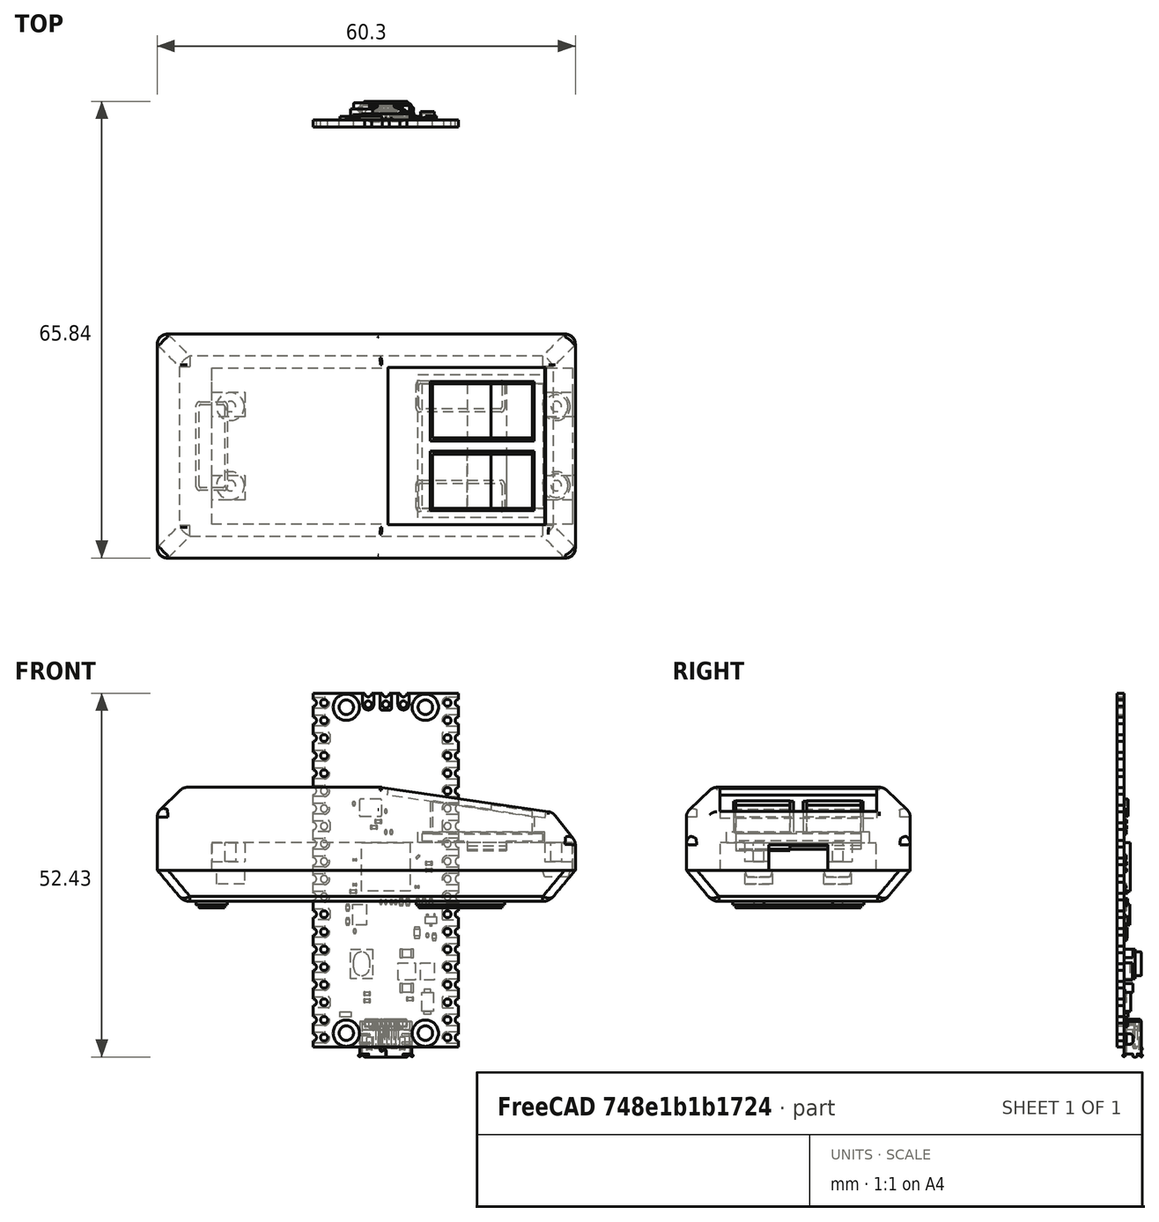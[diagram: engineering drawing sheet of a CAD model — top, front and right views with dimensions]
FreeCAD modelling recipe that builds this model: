
FCSTD DOCUMENT  (FreeCAD 0.22R36731 (Git))
Label: mouse
License: All rights reserved
LicenseURL: http://en.wikipedia.org/wiki/All_rights_reserved
objects: Part::Feature×116, App::Part×35, Sketcher::SketchObject×19, PartDesign::Pocket×11, PartDesign::Pad×8, PartDesign::Body×4, PartDesign::Fillet×2, Mesh::Feature×1, PartDesign::Plane×1
note: 182 computed .brp shape members not serialized (recipe doc carries the construction recipe); baked Part::Feature solids carry a one-line shape summary decoded from their .brp

FEATURE [Sketcher::SketchObject] Sketch
  AttachmentSupport = -> [XZ_Plane]
  FullyConstrained = true
  MapMode = 5
  Placement = pos=(0,0,0) rot=(1,0,0;1.5708rad)
  sketch-geometry (14):
    g0: LineSegment StartX=21.1514 StartY=8.48067 StartZ=0 EndX=15.1514 EndY=9.36067 EndZ=0
    g1: LineSegment StartX=15.1514 StartY=9.36067 StartZ=0 EndX=15.1514 EndY=8.76067 EndZ=0
    g2: LineSegment StartX=15.1514 StartY=8.76067 StartZ=0 EndX=6.70138 EndY=10 EndZ=0
    g3: LineSegment StartX=6.70138 StartY=10 StartZ=0 EndX=6.70138 EndY=5.25 EndZ=0
    g4: LineSegment StartX=6.70138 StartY=5.25 StartZ=0 EndX=5.20138 EndY=5.25 EndZ=0
    g5: LineSegment StartX=5.20138 StartY=5.25 StartZ=0 EndX=5.20138 EndY=4.25 EndZ=0
    g6: LineSegment StartX=5.20138 StartY=4.25 StartZ=0 EndX=11.74 EndY=4.25 EndZ=0
    g7: LineSegment StartX=11.74 StartY=4.25 StartZ=0 EndX=11.74 EndY=3 EndZ=0
    g8: LineSegment StartX=11.74 StartY=3 StartZ=0 EndX=17.37 EndY=3 EndZ=0
    g9: LineSegment StartX=17.37 StartY=3 StartZ=0 EndX=17.37 EndY=4.25 EndZ=0
    g10: LineSegment StartX=17.37 StartY=4.25 StartZ=0 EndX=22.6514 EndY=4.25 EndZ=0
    g11: LineSegment StartX=22.6514 StartY=4.25 StartZ=0 EndX=22.6514 EndY=5.25 EndZ=0
    g12: LineSegment StartX=22.6514 StartY=5.25 StartZ=0 EndX=21.1514 EndY=5.25 EndZ=0
    g13: LineSegment StartX=21.1514 StartY=5.25 StartZ=0 EndX=21.1514 EndY=8.48067 EndZ=0
  constraints (42):
    c: Coincident(g0,g1)
    c: Vertical(g1)
    c: Coincident(g1,g2)
    c: Coincident(g2,g3)
    c: Vertical(g3)
    c: Coincident(g3,g4)
    c: Coincident(g4,g5)
    c: Vertical(g5)
    c: Coincident(g5,g6)
    c: Horizontal(g6)
    c: Coincident(g6,g7)
    c: Coincident(g7,g8)
    c: Horizontal(g8)
    c: Coincident(g8,g9)
    c: Coincident(g9,g10)
    c: Coincident(g10,g11)
    c: Vertical(g11)
    c: Coincident(g11,g12)
    c: Coincident(g12,g13)
    c: Coincident(g13,g0)
    c: Vertical(g13)
    c: Parallel(g0,g2)
    c: DistanceX(g0) = 21.1514
    c: DistanceX(g0,g0) = 6
    c: DistanceX(g2,g2) = 8.45
    c: DistanceY(g0,g0) = 0.88
    c: DistanceY(g1,g1) = 0.6
    c: Vertical(g9)
    c: Vertical(g7)
    c: Horizontal(g10)
    c: Equal(g7,g9)
    c: DistanceX(g7) = 11.74
    c: DistanceX(g8,g8) = 5.63
    c: DistanceX(g4,g3) = 1.5
    c: DistanceY(g7) = 3
    c: Horizontal(g12)
    c: DistanceX(g12,g12) = 1.5
    c: Horizontal(g4)
    c: PointOnObject(g3,g12)
    c: DistanceY(g5,g5) = 1
    c: DistanceY(g7,g7) = 1.25
    c: DistanceY(g3,g3) = 4.75
FEATURE [PartDesign::Pad] Pad
  Direction = (0,-1,2e-16)
  Length = 18
  Length2 = 10
  Placement = pos=(0,0,0) rot=(1,0,0;1.5708rad)
  Profile = -> Sketch
  ReferenceAxis = -> Sketch [N_Axis]
  Refine = true
  Suppressed = false
  Type = 0
FEATURE [Mesh::Feature] mouse_bottom
FEATURE [Part::Feature] Part__Feature  label="PCB, Raspberry Pi Pico-R3"
  shape: bbox 21 x 1 x 51 mm, 416 faces (baked)
FEATURE [Part::Feature] Part__Feature001  label="MicroUSB Port, Raspberry Pi Pico-R3"
  Placement = pos=(0,0.5,-24.35) rot=(0,1,0;3.14159rad)
  shape: bbox 7.999 x 2.949 x 5.461 mm, 809 faces (baked)
FEATURE [Part::Feature] Part__Feature002  label="MicroUSB Port, Raspberry Pi Pico-R004"
  Placement = pos=(0,0.5,-24.35) rot=(0,1,0;3.14159rad)
  shape: bbox 6.982 x 2.155 x 3.937 mm, 206 faces (baked)
FEATURE [Part::Feature] Part__Feature003  label="MicroUSB Port, Raspberry Pi Pico-R005"
  Placement = pos=(0,0.5,-24.35) rot=(0,1,0;3.14159rad)
  shape: bbox 0.37 x 1.716 x 4 mm, 43 faces (baked)
FEATURE [Part::Feature] Part__Feature004  label="MicroUSB Port, Raspberry Pi Pico-R006"
  Placement = pos=(0,0.5,-24.35) rot=(0,1,0;3.14159rad)
  shape: bbox 0.37 x 1.716 x 4 mm, 43 faces (baked)
FEATURE [Part::Feature] Part__Feature005  label="MicroUSB Port, Raspberry Pi Pico-R007"
  Placement = pos=(0,0.5,-24.35) rot=(0,1,0;3.14159rad)
  shape: bbox 0.37 x 1.716 x 4 mm, 43 faces (baked)
FEATURE [Part::Feature] Part__Feature006  label="MicroUSB Port, Raspberry Pi Pico-R008"
  Placement = pos=(0,0.5,-24.35) rot=(0,1,0;3.14159rad)
  shape: bbox 0.37 x 1.716 x 4 mm, 43 faces (baked)
FEATURE [Part::Feature] Part__Feature007  label="MicroUSB Port, Raspberry Pi Pico-R009"
  Placement = pos=(0,0.5,-24.35) rot=(0,1,0;3.14159rad)
  shape: bbox 0.37 x 1.716 x 4 mm, 43 faces (baked)
FEATURE [App::Part] MicroUSB_Port__Raspberry_Pi_Pico_R3  label="MicroUSB Port, Raspberry Pi Pico-R010"
  Group = -> [Part__Feature001,Part__Feature002,Part__Feature003,Part__Feature004,Part__Feature005,Part__Feature006,Part__Feature007]
  Origin = -> Origin001
FEATURE [Part::Feature] Part__Feature008  label="RP2040 Microcontroller, Raspberry Pi Pico-R3"
  Placement = pos=(0,0.5,0.5) rot=(0,0,1;0rad)
  shape: bbox 7 x 0.9 x 7 mm, 6 faces (baked)
FEATURE [Part::Feature] Part__Feature009  label="SW1, Tact Switch, Raspberry Pi Pico-R3"
  Placement = pos=(-3.5,0.5,-13.5) rot=(0,0,1;0rad)
  shape: bbox 3.2 x 2.5 x 4.25 mm, 17 faces (baked)
FEATURE [Part::Feature] Part__Feature010  label="D1, Diode, Schottky, Raspberry Pi Pico-R3"
  Placement = pos=(6,0.5,-19) rot=(0,0,1;0rad)
  shape: bbox 1.65 x 0.95 x 3.6 mm, 14 faces (baked)
FEATURE [Part::Feature] Part__Feature011  label="D2, QSME-C194, LED, Raspberry Pi Pico-R3"
  Placement = pos=(-5.8,0.5,-20.8) rot=(0,0,1;0rad)
  shape: bbox 1.6 x 0.55 x 0.8 mm, 6 faces (baked)
FEATURE [Part::Feature] Part__Feature012  label="L1, Inductor, Raspberry Pi Pico-R3"
  Placement = pos=(6,0.5,-14.6) rot=(0,0,1;0rad)
  shape: bbox 2 x 1.2 x 2.5 mm, 6 faces (baked)
FEATURE [Part::Feature] Part__Feature013  label="U2, RT6150B-33GQW, Buck Boost Converter, Raspberry Pi Pico-R3"
  Placement = pos=(3,0.5,-14.6) rot=(0,0,1;0rad)
  shape: bbox 2.5 x 0.8 x 2.5 mm, 6 faces (baked)
FEATURE [Part::Feature] Part__Feature014  label="U3, W25Q16JVUXIQ, Serial NOR Flash 16 Mbit, Raspberry Pi Pico-R3"
  Placement = pos=(-3.8,0.5,-6.4) rot=(0,0,1;0rad)
  shape: bbox 2 x 0.8 x 3 mm, 6 faces (baked)
FEATURE [Part::Feature] Part__Feature015  label="Q1, MOSFET, DMG1012T, Raspberry Pi Pico-R3"
  Placement = pos=(6.5,0.5,-7.2) rot=(0,0,1;0rad)
  shape: bbox 1.6 x 0.6 x 1.8 mm, 18 faces (baked)
FEATURE [Part::Feature] Part__Feature016  label="X1, X12M000000S096, 12 Mhz Crystal Resonator, Raspberry Pi Pico-R3"
  Placement = pos=(-2.2,0.5,9) rot=(0,0,1;0rad)
  shape: bbox 3.2 x 0.6 x 2.5 mm, 18 faces (baked)
FEATURE [Part::Feature] Part__Feature017  label="SMD Resistor, Configurable, Raspberry Pi Pico-R3_R1"
  Placement = pos=(6.2,0.5,1) rot=(0,1,0;1.5708rad)
  shape: bbox 0.6 x 0.35 x 0.5 mm, 6 faces (baked)
FEATURE [Part::Feature] Part__Feature018  label="SMD Resistor, Configurable, Raspberry Pi Pico-R3_R002"
  Placement = pos=(6.2,0.5,1) rot=(0,1,0;1.5708rad)
  shape: bbox 0.2 x 0.35 x 0.5 mm, 6 faces (baked)
FEATURE [Part::Feature] Part__Feature019  label="SMD Resistor, Configurable, Raspberry Pi Pico-R3_R003"
  Placement = pos=(6.2,0.5,1) rot=(0,1,0;1.5708rad)
  shape: bbox 0.2 x 0.35 x 0.5 mm, 6 faces (baked)
FEATURE [App::Part] SMD_Resistor__Configurable__Raspberry_Pi_Pico_R3_R1  label="SMD Resistor, Configurable, Raspberry Pi Pico-R3_R004"
  Group = -> [Part__Feature017,Part__Feature018,Part__Feature019]
  Origin = -> Origin002
FEATURE [Part::Feature] Part__Feature020  label="SMD Resistor, Configurable, Raspberry Pi Pico-R3_R2"
  Placement = pos=(3.5,0.5,-18.6) rot=(0,1,0;1.5708rad)
  shape: bbox 0.6 x 0.35 x 0.5 mm, 6 faces (baked)
FEATURE [Part::Feature] Part__Feature021  label="SMD Resistor, Configurable, Raspberry Pi Pico-R3_R005"
  Placement = pos=(3.5,0.5,-18.6) rot=(0,1,0;1.5708rad)
  shape: bbox 0.2 x 0.35 x 0.5 mm, 6 faces (baked)
FEATURE [Part::Feature] Part__Feature022  label="SMD Resistor, Configurable, Raspberry Pi Pico-R3_R006"
  Placement = pos=(3.5,0.5,-18.6) rot=(0,1,0;1.5708rad)
  shape: bbox 0.2 x 0.35 x 0.5 mm, 6 faces (baked)
FEATURE [App::Part] SMD_Resistor__Configurable__Raspberry_Pi_Pico_R3_R2  label="SMD Resistor, Configurable, Raspberry Pi Pico-R3_R007"
  Group = -> [Part__Feature020,Part__Feature021,Part__Feature022]
  Origin = -> Origin003
FEATURE [Part::Feature] Part__Feature023  label="SMD Resistor, Configurable, Raspberry Pi Pico-R3_R3"
  Placement = pos=(-2.7,0.5,-17.8) rot=(0,1,0;1.5708rad)
  shape: bbox 0.6 x 0.35 x 0.5 mm, 6 faces (baked)
FEATURE [Part::Feature] Part__Feature024  label="SMD Resistor, Configurable, Raspberry Pi Pico-R3_R008"
  Placement = pos=(-2.7,0.5,-17.8) rot=(0,1,0;1.5708rad)
  shape: bbox 0.2 x 0.35 x 0.5 mm, 6 faces (baked)
FEATURE [Part::Feature] Part__Feature025  label="SMD Resistor, Configurable, Raspberry Pi Pico-R3_R009"
  Placement = pos=(-2.7,0.5,-17.8) rot=(0,1,0;1.5708rad)
  shape: bbox 0.2 x 0.35 x 0.5 mm, 6 faces (baked)
FEATURE [App::Part] SMD_Resistor__Configurable__Raspberry_Pi_Pico_R3_R3  label="SMD Resistor, Configurable, Raspberry Pi Pico-R3_R010"
  Group = -> [Part__Feature023,Part__Feature024,Part__Feature025]
  Origin = -> Origin004
FEATURE [Part::Feature] Part__Feature026  label="SMD Resistor, Configurable, Raspberry Pi Pico-R3_R4"
  Placement = pos=(-5.5,0.5,-5.4) rot=(0,1,0;3.14159rad)
  shape: bbox 0.5 x 0.35 x 0.6 mm, 6 faces (baked)
FEATURE [Part::Feature] Part__Feature027  label="SMD Resistor, Configurable, Raspberry Pi Pico-R3_R011"
  Placement = pos=(-5.5,0.5,-5.4) rot=(0,1,0;3.14159rad)
  shape: bbox 0.5 x 0.35 x 0.2 mm, 6 faces (baked)
FEATURE [Part::Feature] Part__Feature028  label="SMD Resistor, Configurable, Raspberry Pi Pico-R3_R012"
  Placement = pos=(-5.5,0.5,-5.4) rot=(0,1,0;3.14159rad)
  shape: bbox 0.5 x 0.35 x 0.2 mm, 6 faces (baked)
FEATURE [App::Part] SMD_Resistor__Configurable__Raspberry_Pi_Pico_R3_R4  label="SMD Resistor, Configurable, Raspberry Pi Pico-R3_R013"
  Group = -> [Part__Feature026,Part__Feature027,Part__Feature028]
  Origin = -> Origin005
FEATURE [Part::Feature] Part__Feature029  label="SMD Resistor, Configurable, Raspberry Pi Pico-R3_R5"
  Placement = pos=(7,0.5,-9.6) rot=(0,1,0;3.14159rad)
  shape: bbox 0.5 x 0.35 x 0.6 mm, 6 faces (baked)
FEATURE [Part::Feature] Part__Feature030  label="SMD Resistor, Configurable, Raspberry Pi Pico-R3_R014"
  Placement = pos=(7,0.5,-9.6) rot=(0,1,0;3.14159rad)
  shape: bbox 0.5 x 0.35 x 0.2 mm, 6 faces (baked)
FEATURE [Part::Feature] Part__Feature031  label="SMD Resistor, Configurable, Raspberry Pi Pico-R3_R015"
  Placement = pos=(7,0.5,-9.6) rot=(0,1,0;3.14159rad)
  shape: bbox 0.5 x 0.35 x 0.2 mm, 6 faces (baked)
FEATURE [App::Part] SMD_Resistor__Configurable__Raspberry_Pi_Pico_R3_R5  label="SMD Resistor, Configurable, Raspberry Pi Pico-R3_R016"
  Group = -> [Part__Feature029,Part__Feature030,Part__Feature031]
  Origin = -> Origin006
FEATURE [Part::Feature] Part__Feature032  label="SMD Resistor, Configurable, Raspberry Pi Pico-R3_R6"
  Placement = pos=(6.5,0.5,-4.6) rot=(0,1,0;3.14159rad)
  shape: bbox 0.5 x 0.35 x 0.6 mm, 6 faces (baked)
FEATURE [Part::Feature] Part__Feature033  label="SMD Resistor, Configurable, Raspberry Pi Pico-R3_R017"
  Placement = pos=(6.5,0.5,-4.6) rot=(0,1,0;3.14159rad)
  shape: bbox 0.5 x 0.35 x 0.2 mm, 6 faces (baked)
FEATURE [Part::Feature] Part__Feature034  label="SMD Resistor, Configurable, Raspberry Pi Pico-R3_R018"
  Placement = pos=(6.5,0.5,-4.6) rot=(0,1,0;3.14159rad)
  shape: bbox 0.5 x 0.35 x 0.2 mm, 6 faces (baked)
FEATURE [App::Part] SMD_Resistor__Configurable__Raspberry_Pi_Pico_R3_R6  label="SMD Resistor, Configurable, Raspberry Pi Pico-R3_R019"
  Group = -> [Part__Feature032,Part__Feature033,Part__Feature034]
  Origin = -> Origin007
FEATURE [Part::Feature] Part__Feature035  label="SMD Resistor, Configurable, Raspberry Pi Pico-R3_R7"
  Placement = pos=(4.5,0.5,-9) rot=(0,1,0;3.14159rad)
  shape: bbox 0.8 x 0.45 x 1 mm, 6 faces (baked)
FEATURE [Part::Feature] Part__Feature036  label="SMD Resistor, Configurable, Raspberry Pi Pico-R3_R020"
  Placement = pos=(4.5,0.5,-9) rot=(0,1,0;3.14159rad)
  shape: bbox 0.8 x 0.45 x 0.3 mm, 6 faces (baked)
FEATURE [Part::Feature] Part__Feature037  label="SMD Resistor, Configurable, Raspberry Pi Pico-R3_R021"
  Placement = pos=(4.5,0.5,-9) rot=(0,1,0;3.14159rad)
  shape: bbox 0.8 x 0.45 x 0.3 mm, 6 faces (baked)
FEATURE [App::Part] SMD_Resistor__Configurable__Raspberry_Pi_Pico_R3_R7  label="SMD Resistor, Configurable, Raspberry Pi Pico-R3_R022"
  Group = -> [Part__Feature035,Part__Feature036,Part__Feature037]
  Origin = -> Origin008
FEATURE [Part::Feature] Part__Feature038  label="SMD Resistor, Configurable, Raspberry Pi Pico-R3_R8"
  Placement = pos=(-2.7,0.5,-18.8) rot=(0,1,0;1.5708rad)
  shape: bbox 0.6 x 0.35 x 0.5 mm, 6 faces (baked)
FEATURE [Part::Feature] Part__Feature039  label="SMD Resistor, Configurable, Raspberry Pi Pico-R3_R023"
  Placement = pos=(-2.7,0.5,-18.8) rot=(0,1,0;1.5708rad)
  shape: bbox 0.2 x 0.35 x 0.5 mm, 6 faces (baked)
FEATURE [Part::Feature] Part__Feature040  label="SMD Resistor, Configurable, Raspberry Pi Pico-R3_R024"
  Placement = pos=(-2.7,0.5,-18.8) rot=(0,1,0;1.5708rad)
  shape: bbox 0.2 x 0.35 x 0.5 mm, 6 faces (baked)
FEATURE [App::Part] SMD_Resistor__Configurable__Raspberry_Pi_Pico_R3_R8  label="SMD Resistor, Configurable, Raspberry Pi Pico-R3_R025"
  Group = -> [Part__Feature038,Part__Feature039,Part__Feature040]
  Origin = -> Origin009
FEATURE [Part::Feature] Part__Feature041  label="SMD Resistor, Configurable, Raspberry Pi Pico-R3_R9"
  Placement = pos=(5.5,0.5,-4.6) rot=(0,1,0;3.14159rad)
  shape: bbox 0.5 x 0.35 x 0.6 mm, 6 faces (baked)
FEATURE [Part::Feature] Part__Feature042  label="SMD Resistor, Configurable, Raspberry Pi Pico-R3_R026"
  Placement = pos=(5.5,0.5,-4.6) rot=(0,1,0;3.14159rad)
  shape: bbox 0.5 x 0.35 x 0.2 mm, 6 faces (baked)
FEATURE [Part::Feature] Part__Feature043  label="SMD Resistor, Configurable, Raspberry Pi Pico-R3_R027"
  Placement = pos=(5.5,0.5,-4.6) rot=(0,1,0;3.14159rad)
  shape: bbox 0.5 x 0.35 x 0.2 mm, 6 faces (baked)
FEATURE [App::Part] SMD_Resistor__Configurable__Raspberry_Pi_Pico_R3_R9  label="SMD Resistor, Configurable, Raspberry Pi Pico-R3_R028"
  Group = -> [Part__Feature041,Part__Feature042,Part__Feature043]
  Origin = -> Origin010
FEATURE [Part::Feature] Part__Feature044  label="SMD Resistor, Configurable, Raspberry Pi Pico-R3_R10"
  Placement = pos=(6.2,0.5,-1e-16) rot=(0,1,0;1.5708rad)
  shape: bbox 0.6 x 0.35 x 0.5 mm, 6 faces (baked)
FEATURE [Part::Feature] Part__Feature045  label="SMD Resistor, Configurable, Raspberry Pi Pico-R3_R029"
  Placement = pos=(6.2,0.5,-1e-16) rot=(0,1,0;1.5708rad)
  shape: bbox 0.2 x 0.35 x 0.5 mm, 6 faces (baked)
FEATURE [Part::Feature] Part__Feature046  label="SMD Resistor, Configurable, Raspberry Pi Pico-R3_R030"
  Placement = pos=(6.2,0.5,-1e-16) rot=(0,1,0;1.5708rad)
  shape: bbox 0.2 x 0.35 x 0.5 mm, 6 faces (baked)
FEATURE [App::Part] SMD_Resistor__Configurable__Raspberry_Pi_Pico_R3_R10  label="SMD Resistor, Configurable, Raspberry Pi Pico-R3_R031"
  Group = -> [Part__Feature044,Part__Feature045,Part__Feature046]
  Origin = -> Origin011
FEATURE [Part::Feature] Part__Feature047  label="SMD Resistor, Configurable, Raspberry Pi Pico-R3_R11"
  Placement = pos=(-5.5,0.5,-7.4) rot=(0,0,1;0rad)
  shape: bbox 0.5 x 0.35 x 0.6 mm, 6 faces (baked)
FEATURE [Part::Feature] Part__Feature048  label="SMD Resistor, Configurable, Raspberry Pi Pico-R3_R032"
  Placement = pos=(-5.5,0.5,-7.4) rot=(0,0,1;0rad)
  shape: bbox 0.5 x 0.35 x 0.2 mm, 6 faces (baked)
FEATURE [Part::Feature] Part__Feature049  label="SMD Resistor, Configurable, Raspberry Pi Pico-R3_R033"
  Placement = pos=(-5.5,0.5,-7.4) rot=(0,0,1;0rad)
  shape: bbox 0.5 x 0.35 x 0.2 mm, 6 faces (baked)
FEATURE [App::Part] SMD_Resistor__Configurable__Raspberry_Pi_Pico_R3_R11  label="SMD Resistor, Configurable, Raspberry Pi Pico-R3_R034"
  Group = -> [Part__Feature047,Part__Feature048,Part__Feature049]
  Origin = -> Origin012
FEATURE [Part::Feature] Part__Feature050  label="SMD Resistor, Configurable, Raspberry Pi Pico-R3_R12"
  Placement = pos=(0.8,0.5,-4.6) rot=(0,1,0;3.14159rad)
  shape: bbox 0.3 x 0.23 x 0.4 mm, 6 faces (baked)
FEATURE [Part::Feature] Part__Feature051  label="SMD Resistor, Configurable, Raspberry Pi Pico-R3_R035"
  Placement = pos=(0.8,0.5,-4.6) rot=(0,1,0;3.14159rad)
  shape: bbox 0.3 x 0.23 x 0.1 mm, 6 faces (baked)
FEATURE [Part::Feature] Part__Feature052  label="SMD Resistor, Configurable, Raspberry Pi Pico-R3_R036"
  Placement = pos=(0.8,0.5,-4.6) rot=(0,1,0;3.14159rad)
  shape: bbox 0.3 x 0.23 x 0.1 mm, 6 faces (baked)
FEATURE [App::Part] SMD_Resistor__Configurable__Raspberry_Pi_Pico_R3_R12  label="SMD Resistor, Configurable, Raspberry Pi Pico-R3_R037"
  Group = -> [Part__Feature050,Part__Feature051,Part__Feature052]
  Origin = -> Origin013
FEATURE [Part::Feature] Part__Feature053  label="SMD Resistor, Configurable, Raspberry Pi Pico-R3_R13"
  Placement = pos=(1.4,0.5,-4.6) rot=(0,1,0;3.14159rad)
  shape: bbox 0.3 x 0.23 x 0.4 mm, 6 faces (baked)
FEATURE [Part::Feature] Part__Feature054  label="SMD Resistor, Configurable, Raspberry Pi Pico-R3_R038"
  Placement = pos=(1.4,0.5,-4.6) rot=(0,1,0;3.14159rad)
  shape: bbox 0.3 x 0.23 x 0.1 mm, 6 faces (baked)
FEATURE [Part::Feature] Part__Feature055  label="SMD Resistor, Configurable, Raspberry Pi Pico-R3_R039"
  Placement = pos=(1.4,0.5,-4.6) rot=(0,1,0;3.14159rad)
  shape: bbox 0.3 x 0.23 x 0.1 mm, 6 faces (baked)
FEATURE [App::Part] SMD_Resistor__Configurable__Raspberry_Pi_Pico_R3_R13  label="SMD Resistor, Configurable, Raspberry Pi Pico-R3_R040"
  Group = -> [Part__Feature053,Part__Feature054,Part__Feature055]
  Origin = -> Origin014
FEATURE [Part::Feature] Part__Feature056  label="SMD Resistor, Configurable, Raspberry Pi Pico-R3_R14"
  Placement = pos=(-1.1,0.5,7) rot=(0,1,0;1.5708rad)
  shape: bbox 0.6 x 0.35 x 0.5 mm, 6 faces (baked)
FEATURE [Part::Feature] Part__Feature057  label="SMD Resistor, Configurable, Raspberry Pi Pico-R3_R041"
  Placement = pos=(-1.1,0.5,7) rot=(0,1,0;1.5708rad)
  shape: bbox 0.2 x 0.35 x 0.5 mm, 6 faces (baked)
FEATURE [Part::Feature] Part__Feature058  label="SMD Resistor, Configurable, Raspberry Pi Pico-R3_R042"
  Placement = pos=(-1.1,0.5,7) rot=(0,1,0;1.5708rad)
  shape: bbox 0.2 x 0.35 x 0.5 mm, 6 faces (baked)
FEATURE [App::Part] SMD_Resistor__Configurable__Raspberry_Pi_Pico_R3_R14  label="SMD Resistor, Configurable, Raspberry Pi Pico-R3_R043"
  Group = -> [Part__Feature056,Part__Feature057,Part__Feature058]
  Origin = -> Origin015
FEATURE [Part::Feature] Part__Feature059  label="SMD Resistor, Configurable, Raspberry Pi Pico-R3_R15"
  Placement = pos=(-1.7,0.5,6.2) rot=(0,1,0;1.5708rad)
  shape: bbox 0.6 x 0.35 x 0.5 mm, 6 faces (baked)
FEATURE [Part::Feature] Part__Feature060  label="SMD Resistor, Configurable, Raspberry Pi Pico-R3_R044"
  Placement = pos=(-1.7,0.5,6.2) rot=(0,1,0;1.5708rad)
  shape: bbox 0.2 x 0.35 x 0.5 mm, 6 faces (baked)
FEATURE [Part::Feature] Part__Feature061  label="SMD Resistor, Configurable, Raspberry Pi Pico-R3_R045"
  Placement = pos=(-1.7,0.5,6.2) rot=(0,1,0;1.5708rad)
  shape: bbox 0.2 x 0.35 x 0.5 mm, 6 faces (baked)
FEATURE [App::Part] SMD_Resistor__Configurable__Raspberry_Pi_Pico_R3_R15  label="SMD Resistor, Configurable, Raspberry Pi Pico-R3_R046"
  Group = -> [Part__Feature059,Part__Feature060,Part__Feature061]
  Origin = -> Origin016
FEATURE [Part::Feature] Part__Feature062  label="SMD Capacitor, Configurable, Raspberry Pi Pico-R3_C1"
  Placement = pos=(3,0.5,-17) rot=(0,1,0;1.5708rad)
  shape: bbox 1.2 x 1.25 x 1.25 mm, 6 faces (baked)
FEATURE [Part::Feature] Part__Feature063  label="SMD Capacitor, Configurable, Raspberry Pi Pico-R3_C002"
  Placement = pos=(3,0.5,-17) rot=(0,1,0;1.5708rad)
  shape: bbox 0.4 x 1.25 x 1.25 mm, 6 faces (baked)
FEATURE [Part::Feature] Part__Feature064  label="SMD Capacitor, Configurable, Raspberry Pi Pico-R3_C003"
  Placement = pos=(3,0.5,-17) rot=(0,1,0;1.5708rad)
  shape: bbox 0.4 x 1.25 x 1.25 mm, 6 faces (baked)
FEATURE [App::Part] SMD_Capacitor__Configurable__Raspberry_Pi_Pico_R3_C1  label="SMD Capacitor, Configurable, Raspberry Pi Pico-R3_C004"
  Group = -> [Part__Feature062,Part__Feature063,Part__Feature064]
  Origin = -> Origin017
FEATURE [Part::Feature] Part__Feature065  label="SMD Capacitor, Configurable, Raspberry Pi Pico-R3_C2"
  Placement = pos=(3,0.5,-12) rot=(0,1,0;1.5708rad)
  shape: bbox 1.2 x 1.25 x 1.25 mm, 6 faces (baked)
FEATURE [Part::Feature] Part__Feature066  label="SMD Capacitor, Configurable, Raspberry Pi Pico-R3_C005"
  Placement = pos=(3,0.5,-12) rot=(0,1,0;1.5708rad)
  shape: bbox 0.4 x 1.25 x 1.25 mm, 6 faces (baked)
FEATURE [Part::Feature] Part__Feature067  label="SMD Capacitor, Configurable, Raspberry Pi Pico-R3_C006"
  Placement = pos=(3,0.5,-12) rot=(0,1,0;1.5708rad)
  shape: bbox 0.4 x 1.25 x 1.25 mm, 6 faces (baked)
FEATURE [App::Part] SMD_Capacitor__Configurable__Raspberry_Pi_Pico_R3_C2  label="SMD Capacitor, Configurable, Raspberry Pi Pico-R3_C007"
  Group = -> [Part__Feature065,Part__Feature066,Part__Feature067]
  Origin = -> Origin018
FEATURE [Part::Feature] Part__Feature068  label="SMD Capacitor, Configurable, Raspberry Pi Pico-R3_C3"
  Placement = pos=(6,0.5,-9.4) rot=(0,0,1;0rad)
  shape: bbox 0.3 x 0.3 x 0.4 mm, 6 faces (baked)
FEATURE [Part::Feature] Part__Feature069  label="SMD Capacitor, Configurable, Raspberry Pi Pico-R3_C008"
  Placement = pos=(6,0.5,-9.4) rot=(0,0,1;0rad)
  shape: bbox 0.3 x 0.3 x 0.1 mm, 6 faces (baked)
FEATURE [Part::Feature] Part__Feature070  label="SMD Capacitor, Configurable, Raspberry Pi Pico-R3_C009"
  Placement = pos=(6,0.5,-9.4) rot=(0,0,1;0rad)
  shape: bbox 0.3 x 0.3 x 0.1 mm, 6 faces (baked)
FEATURE [App::Part] SMD_Capacitor__Configurable__Raspberry_Pi_Pico_R3_C3  label="SMD Capacitor, Configurable, Raspberry Pi Pico-R3_C010"
  Group = -> [Part__Feature068,Part__Feature069,Part__Feature070]
  Origin = -> Origin019
FEATURE [Part::Feature] Part__Feature071  label="SMD Capacitor, Configurable, Raspberry Pi Pico-R3_C4"
  Placement = pos=(-4.5,0.5,-2.1) rot=(0,-1,0;1.5708rad)
  shape: bbox 0.4 x 0.3 x 0.3 mm, 6 faces (baked)
FEATURE [Part::Feature] Part__Feature072  label="SMD Capacitor, Configurable, Raspberry Pi Pico-R3_C011"
  Placement = pos=(-4.5,0.5,-2.1) rot=(0,-1,0;1.5708rad)
  shape: bbox 0.1 x 0.3 x 0.3 mm, 6 faces (baked)
FEATURE [Part::Feature] Part__Feature073  label="SMD Capacitor, Configurable, Raspberry Pi Pico-R3_C012"
  Placement = pos=(-4.5,0.5,-2.1) rot=(0,-1,0;1.5708rad)
  shape: bbox 0.1 x 0.3 x 0.3 mm, 6 faces (baked)
FEATURE [App::Part] SMD_Capacitor__Configurable__Raspberry_Pi_Pico_R3_C4  label="SMD Capacitor, Configurable, Raspberry Pi Pico-R3_C013"
  Group = -> [Part__Feature071,Part__Feature072,Part__Feature073]
  Origin = -> Origin020
FEATURE [Part::Feature] Part__Feature074  label="SMD Capacitor, Configurable, Raspberry Pi Pico-R3_C5"
  Placement = pos=(-4.5,0.5,1.5) rot=(0,-1,0;1.5708rad)
  shape: bbox 0.4 x 0.3 x 0.3 mm, 6 faces (baked)
FEATURE [Part::Feature] Part__Feature075  label="SMD Capacitor, Configurable, Raspberry Pi Pico-R3_C014"
  Placement = pos=(-4.5,0.5,1.5) rot=(0,-1,0;1.5708rad)
  shape: bbox 0.1 x 0.3 x 0.3 mm, 6 faces (baked)
FEATURE [Part::Feature] Part__Feature076  label="SMD Capacitor, Configurable, Raspberry Pi Pico-R3_C015"
  Placement = pos=(-4.5,0.5,1.5) rot=(0,-1,0;1.5708rad)
  shape: bbox 0.1 x 0.3 x 0.3 mm, 6 faces (baked)
FEATURE [App::Part] SMD_Capacitor__Configurable__Raspberry_Pi_Pico_R3_C5  label="SMD Capacitor, Configurable, Raspberry Pi Pico-R3_C016"
  Group = -> [Part__Feature074,Part__Feature075,Part__Feature076]
  Origin = -> Origin021
FEATURE [Part::Feature] Part__Feature077  label="SMD Capacitor, Configurable, Raspberry Pi Pico-R3_C6"
  Placement = pos=(4.6,0.5,1.9) rot=(0,1,0;0.785398rad)
  shape: bbox 0.495 x 0.3 x 0.495 mm, 6 faces (baked)
FEATURE [Part::Feature] Part__Feature078  label="SMD Capacitor, Configurable, Raspberry Pi Pico-R3_C017"
  Placement = pos=(4.6,0.5,1.9) rot=(0,1,0;0.785398rad)
  shape: bbox 0.2828 x 0.3 x 0.2828 mm, 6 faces (baked)
FEATURE [Part::Feature] Part__Feature079  label="SMD Capacitor, Configurable, Raspberry Pi Pico-R3_C018"
  Placement = pos=(4.6,0.5,1.9) rot=(0,1,0;0.785398rad)
  shape: bbox 0.2828 x 0.3 x 0.2828 mm, 6 faces (baked)
FEATURE [App::Part] SMD_Capacitor__Configurable__Raspberry_Pi_Pico_R3_C6  label="SMD Capacitor, Configurable, Raspberry Pi Pico-R3_C019"
  Group = -> [Part__Feature077,Part__Feature078,Part__Feature079]
  Origin = -> Origin022
FEATURE [Part::Feature] Part__Feature080  label="SMD Capacitor, Configurable, Raspberry Pi Pico-R3_C7"
  Placement = pos=(4.5,0.5,-2.4) rot=(0,-1,0;1.5708rad)
  shape: bbox 0.4 x 0.3 x 0.3 mm, 6 faces (baked)
FEATURE [Part::Feature] Part__Feature081  label="SMD Capacitor, Configurable, Raspberry Pi Pico-R3_C020"
  Placement = pos=(4.5,0.5,-2.4) rot=(0,-1,0;1.5708rad)
  shape: bbox 0.1 x 0.3 x 0.3 mm, 6 faces (baked)
FEATURE [Part::Feature] Part__Feature082  label="SMD Capacitor, Configurable, Raspberry Pi Pico-R3_C021"
  Placement = pos=(4.5,0.5,-2.4) rot=(0,-1,0;1.5708rad)
  shape: bbox 0.1 x 0.3 x 0.3 mm, 6 faces (baked)
FEATURE [App::Part] SMD_Capacitor__Configurable__Raspberry_Pi_Pico_R3_C7  label="SMD Capacitor, Configurable, Raspberry Pi Pico-R3_C022"
  Group = -> [Part__Feature080,Part__Feature081,Part__Feature082]
  Origin = -> Origin023
FEATURE [Part::Feature] Part__Feature083  label="SMD Capacitor, Configurable, Raspberry Pi Pico-R3_C8"
  Placement = pos=(0,0.5,5.5) rot=(0,0,1;0rad)
  shape: bbox 0.3 x 0.3 x 0.4 mm, 6 faces (baked)
FEATURE [Part::Feature] Part__Feature084  label="SMD Capacitor, Configurable, Raspberry Pi Pico-R3_C023"
  Placement = pos=(0,0.5,5.5) rot=(0,0,1;0rad)
  shape: bbox 0.3 x 0.3 x 0.1 mm, 6 faces (baked)
FEATURE [Part::Feature] Part__Feature085  label="SMD Capacitor, Configurable, Raspberry Pi Pico-R3_C024"
  Placement = pos=(0,0.5,5.5) rot=(0,0,1;0rad)
  shape: bbox 0.3 x 0.3 x 0.1 mm, 6 faces (baked)
FEATURE [App::Part] SMD_Capacitor__Configurable__Raspberry_Pi_Pico_R3_C8  label="SMD Capacitor, Configurable, Raspberry Pi Pico-R3_C025"
  Group = -> [Part__Feature083,Part__Feature084,Part__Feature085]
  Origin = -> Origin024
FEATURE [Part::Feature] Part__Feature086  label="SMD Capacitor, Configurable, Raspberry Pi Pico-R3_C9"
  Placement = pos=(0.8,0.5,5.5) rot=(0,0,1;0rad)
  shape: bbox 0.3 x 0.3 x 0.4 mm, 6 faces (baked)
FEATURE [Part::Feature] Part__Feature087  label="SMD Capacitor, Configurable, Raspberry Pi Pico-R3_C026"
  Placement = pos=(0.8,0.5,5.5) rot=(0,0,1;0rad)
  shape: bbox 0.3 x 0.3 x 0.1 mm, 6 faces (baked)
FEATURE [Part::Feature] Part__Feature088  label="SMD Capacitor, Configurable, Raspberry Pi Pico-R3_C027"
  Placement = pos=(0.8,0.5,5.5) rot=(0,0,1;0rad)
  shape: bbox 0.3 x 0.3 x 0.1 mm, 6 faces (baked)
FEATURE [App::Part] SMD_Capacitor__Configurable__Raspberry_Pi_Pico_R3_C9  label="SMD Capacitor, Configurable, Raspberry Pi Pico-R3_C028"
  Group = -> [Part__Feature086,Part__Feature087,Part__Feature088]
  Origin = -> Origin025
FEATURE [Part::Feature] Part__Feature089  label="SMD Capacitor, Configurable, Raspberry Pi Pico-R3_C10"
  Placement = pos=(0,0.5,-4.6) rot=(0,0,1;0rad)
  shape: bbox 0.3 x 0.3 x 0.4 mm, 6 faces (baked)
FEATURE [Part::Feature] Part__Feature090  label="SMD Capacitor, Configurable, Raspberry Pi Pico-R3_C029"
  Placement = pos=(0,0.5,-4.6) rot=(0,0,1;0rad)
  shape: bbox 0.3 x 0.3 x 0.1 mm, 6 faces (baked)
FEATURE [Part::Feature] Part__Feature091  label="SMD Capacitor, Configurable, Raspberry Pi Pico-R3_C030"
  Placement = pos=(0,0.5,-4.6) rot=(0,0,1;0rad)
  shape: bbox 0.3 x 0.3 x 0.1 mm, 6 faces (baked)
FEATURE [App::Part] SMD_Capacitor__Configurable__Raspberry_Pi_Pico_R3_C10  label="SMD Capacitor, Configurable, Raspberry Pi Pico-R3_C031"
  Group = -> [Part__Feature089,Part__Feature090,Part__Feature091]
  Origin = -> Origin026
FEATURE [Part::Feature] Part__Feature092  label="SMD Capacitor, Configurable, Raspberry Pi Pico-R3_C11"
  Placement = pos=(-0.7,0.5,-4.6) rot=(0,0,1;0rad)
  shape: bbox 0.3 x 0.3 x 0.4 mm, 6 faces (baked)
FEATURE [Part::Feature] Part__Feature093  label="SMD Capacitor, Configurable, Raspberry Pi Pico-R3_C032"
  Placement = pos=(-0.7,0.5,-4.6) rot=(0,0,1;0rad)
  shape: bbox 0.3 x 0.3 x 0.1 mm, 6 faces (baked)
FEATURE [Part::Feature] Part__Feature094  label="SMD Capacitor, Configurable, Raspberry Pi Pico-R3_C033"
  Placement = pos=(-0.7,0.5,-4.6) rot=(0,0,1;0rad)
  shape: bbox 0.3 x 0.3 x 0.1 mm, 6 faces (baked)
FEATURE [App::Part] SMD_Capacitor__Configurable__Raspberry_Pi_Pico_R3_C11  label="SMD Capacitor, Configurable, Raspberry Pi Pico-R3_C034"
  Group = -> [Part__Feature092,Part__Feature093,Part__Feature094]
  Origin = -> Origin027
FEATURE [Part::Feature] Part__Feature095  label="SMD Capacitor, Configurable, Raspberry Pi Pico-R3_C12"
  Placement = pos=(2.2,0.5,-4.6) rot=(0,0,1;0rad)
  shape: bbox 0.5 x 0.5 x 0.6 mm, 6 faces (baked)
FEATURE [Part::Feature] Part__Feature096  label="SMD Capacitor, Configurable, Raspberry Pi Pico-R3_C035"
  Placement = pos=(2.2,0.5,-4.6) rot=(0,0,1;0rad)
  shape: bbox 0.5 x 0.5 x 0.2 mm, 6 faces (baked)
FEATURE [Part::Feature] Part__Feature097  label="SMD Capacitor, Configurable, Raspberry Pi Pico-R3_C036"
  Placement = pos=(2.2,0.5,-4.6) rot=(0,0,1;0rad)
  shape: bbox 0.5 x 0.5 x 0.2 mm, 6 faces (baked)
FEATURE [App::Part] SMD_Capacitor__Configurable__Raspberry_Pi_Pico_R3_C12  label="SMD Capacitor, Configurable, Raspberry Pi Pico-R3_C037"
  Group = -> [Part__Feature095,Part__Feature096,Part__Feature097]
  Origin = -> Origin028
FEATURE [Part::Feature] Part__Feature098  label="SMD Capacitor, Configurable, Raspberry Pi Pico-R3_C13"
  Placement = pos=(4.6,0.5,-4.6) rot=(0,0,1;0rad)
  shape: bbox 0.5 x 0.5 x 0.6 mm, 6 faces (baked)
FEATURE [Part::Feature] Part__Feature099  label="SMD Capacitor, Configurable, Raspberry Pi Pico-R3_C038"
  Placement = pos=(4.6,0.5,-4.6) rot=(0,0,1;0rad)
  shape: bbox 0.5 x 0.5 x 0.2 mm, 6 faces (baked)
FEATURE [Part::Feature] Part__Feature100  label="SMD Capacitor, Configurable, Raspberry Pi Pico-R3_C039"
  Placement = pos=(4.6,0.5,-4.6) rot=(0,0,1;0rad)
  shape: bbox 0.5 x 0.5 x 0.2 mm, 6 faces (baked)
FEATURE [App::Part] SMD_Capacitor__Configurable__Raspberry_Pi_Pico_R3_C13  label="SMD Capacitor, Configurable, Raspberry Pi Pico-R3_C040"
  Group = -> [Part__Feature098,Part__Feature099,Part__Feature100]
  Origin = -> Origin029
FEATURE [Part::Feature] Part__Feature101  label="SMD Capacitor, Configurable, Raspberry Pi Pico-R3_C14"
  Placement = pos=(3.2,0.5,-4.6) rot=(0,0,1;0rad)
  shape: bbox 0.5 x 0.5 x 0.6 mm, 6 faces (baked)
FEATURE [Part::Feature] Part__Feature102  label="SMD Capacitor, Configurable, Raspberry Pi Pico-R3_C041"
  Placement = pos=(3.2,0.5,-4.6) rot=(0,0,1;0rad)
  shape: bbox 0.5 x 0.5 x 0.2 mm, 6 faces (baked)
FEATURE [Part::Feature] Part__Feature103  label="SMD Capacitor, Configurable, Raspberry Pi Pico-R3_C042"
  Placement = pos=(3.2,0.5,-4.6) rot=(0,0,1;0rad)
  shape: bbox 0.5 x 0.5 x 0.2 mm, 6 faces (baked)
FEATURE [App::Part] SMD_Capacitor__Configurable__Raspberry_Pi_Pico_R3_C14  label="SMD Capacitor, Configurable, Raspberry Pi Pico-R3_C043"
  Group = -> [Part__Feature101,Part__Feature102,Part__Feature103]
  Origin = -> Origin030
FEATURE [Part::Feature] Part__Feature104  label="SMD Capacitor, Configurable, Raspberry Pi Pico-R3_C15"
  Placement = pos=(-4.5,0.5,-8.8) rot=(0,0,1;0rad)
  shape: bbox 0.3 x 0.3 x 0.4 mm, 6 faces (baked)
FEATURE [Part::Feature] Part__Feature105  label="SMD Capacitor, Configurable, Raspberry Pi Pico-R3_C044"
  Placement = pos=(-4.5,0.5,-8.8) rot=(0,0,1;0rad)
  shape: bbox 0.3 x 0.3 x 0.1 mm, 6 faces (baked)
FEATURE [Part::Feature] Part__Feature106  label="SMD Capacitor, Configurable, Raspberry Pi Pico-R3_C045"
  Placement = pos=(-4.5,0.5,-8.8) rot=(0,0,1;0rad)
  shape: bbox 0.3 x 0.3 x 0.1 mm, 6 faces (baked)
FEATURE [App::Part] SMD_Capacitor__Configurable__Raspberry_Pi_Pico_R3_C15  label="SMD Capacitor, Configurable, Raspberry Pi Pico-R3_C046"
  Group = -> [Part__Feature104,Part__Feature105,Part__Feature106]
  Origin = -> Origin031
FEATURE [Part::Feature] Part__Feature107  label="SMD Capacitor, Configurable, Raspberry Pi Pico-R3_C16"
  Placement = pos=(-4.6,0.5,9.6) rot=(0,0,1;0rad)
  shape: bbox 0.3 x 0.3 x 0.4 mm, 6 faces (baked)
FEATURE [Part::Feature] Part__Feature108  label="SMD Capacitor, Configurable, Raspberry Pi Pico-R3_C047"
  Placement = pos=(-4.6,0.5,9.6) rot=(0,0,1;0rad)
  shape: bbox 0.3 x 0.3 x 0.1 mm, 6 faces (baked)
FEATURE [Part::Feature] Part__Feature109  label="SMD Capacitor, Configurable, Raspberry Pi Pico-R3_C048"
  Placement = pos=(-4.6,0.5,9.6) rot=(0,0,1;0rad)
  shape: bbox 0.3 x 0.3 x 0.1 mm, 6 faces (baked)
FEATURE [App::Part] SMD_Capacitor__Configurable__Raspberry_Pi_Pico_R3_C16  label="SMD Capacitor, Configurable, Raspberry Pi Pico-R3_C049"
  Group = -> [Part__Feature107,Part__Feature108,Part__Feature109]
  Origin = -> Origin032
FEATURE [Part::Feature] Part__Feature110  label="SMD Capacitor, Configurable, Raspberry Pi Pico-R3_C17"
  Placement = pos=(0,0.5,8.5) rot=(0,0,1;0rad)
  shape: bbox 0.3 x 0.3 x 0.4 mm, 6 faces (baked)
FEATURE [Part::Feature] Part__Feature111  label="SMD Capacitor, Configurable, Raspberry Pi Pico-R3_C050"
  Placement = pos=(0,0.5,8.5) rot=(0,0,1;0rad)
  shape: bbox 0.3 x 0.3 x 0.1 mm, 6 faces (baked)
FEATURE [Part::Feature] Part__Feature112  label="SMD Capacitor, Configurable, Raspberry Pi Pico-R3_C051"
  Placement = pos=(0,0.5,8.5) rot=(0,0,1;0rad)
  shape: bbox 0.3 x 0.3 x 0.1 mm, 6 faces (baked)
FEATURE [App::Part] SMD_Capacitor__Configurable__Raspberry_Pi_Pico_R3_C17  label="SMD Capacitor, Configurable, Raspberry Pi Pico-R3_C052"
  Group = -> [Part__Feature110,Part__Feature111,Part__Feature112]
  Origin = -> Origin033
FEATURE [Part::Feature] Part__Feature113  label="SMD Capacitor, Configurable, Raspberry Pi Pico-R3_C18"
  Placement = pos=(-4.7,0.5,-3.1) rot=(0,-1,0;1.5708rad)
  shape: bbox 0.6 x 0.5 x 0.5 mm, 6 faces (baked)
FEATURE [Part::Feature] Part__Feature114  label="SMD Capacitor, Configurable, Raspberry Pi Pico-R3_C053"
  Placement = pos=(-4.7,0.5,-3.1) rot=(0,-1,0;1.5708rad)
  shape: bbox 0.2 x 0.5 x 0.5 mm, 6 faces (baked)
FEATURE [Part::Feature] Part__Feature115  label="SMD Capacitor, Configurable, Raspberry Pi Pico-R3_C054"
  Placement = pos=(-4.7,0.5,-3.1) rot=(0,-1,0;1.5708rad)
  shape: bbox 0.2 x 0.5 x 0.5 mm, 6 faces (baked)
FEATURE [App::Part] SMD_Capacitor__Configurable__Raspberry_Pi_Pico_R3_C18  label="SMD Capacitor, Configurable, Raspberry Pi Pico-R3_C055"
  Group = -> [Part__Feature113,Part__Feature114,Part__Feature115]
  Origin = -> Origin034
FEATURE [App::Part] Raspberry_Pi_Pico_R3  label="Raspberry Pi Pico-R3"
  Group = -> [Part__Feature,MicroUSB_Port__Raspberry_Pi_Pico_R3,Part__Feature008,Part__Feature009,Part__Feature010,Part__Feature011,Part__Feature012,Part__Feature013,Part__Feature014,Part__Feature015,Part__Feature016,SMD_Resistor__Configurable__Raspberry_Pi_Pico_R3_R1,SMD_Resistor__Configurable__Raspberry_Pi_Pico_R3_R2,SMD_Resistor__Configurable__Raspberry_Pi_Pico_R3_R3,+30 more]
  Origin = -> Origin035
  Placement = pos=(1.1,-46.38,1.03e-14) rot=(-0.57735,0.57735,0.57735;4.18879rad)
FEATURE [Sketcher::SketchObject] Sketch001
  AttachmentSupport = -> [XZ_Plane036]
  FullyConstrained = false
  MapMode = 5
  Placement = pos=(0,0,0) rot=(1,0,0;1.5708rad)
  sketch-geometry (7):
    g0: LineSegment StartX=-32.9638 StartY=0 StartZ=0 EndX=-32.9638 EndY=8.29425 EndZ=0
    g1: LineSegment StartX=-32.9638 StartY=8.29425 StartZ=0 EndX=-29.2299 EndY=11.9502 EndZ=0
    g2: LineSegment StartX=-29.2299 StartY=11.9502 StartZ=0 EndX=-0.678443 EndY=11.9502 EndZ=0
    g3: LineSegment StartX=-0.678443 StartY=11.9502 StartZ=0 EndX=24.0566 EndY=8.34824 EndZ=0
    g4: LineSegment StartX=24.0566 StartY=8.34824 StartZ=0 EndX=27.3377 EndY=4.14725 EndZ=0
    g5: LineSegment StartX=27.3377 StartY=4.14725 StartZ=0 EndX=27.3377 EndY=0 EndZ=0
    g6: LineSegment StartX=27.3377 StartY=0 StartZ=0 EndX=-32.9638 EndY=0 EndZ=0
  constraints (12):
    c: PointOnObject(g0,g-1)
    c: Vertical(g0)
    c: Coincident(g0,g1)
    c: Coincident(g1,g2)
    c: Horizontal(g2)
    c: Coincident(g2,g3)
    c: Coincident(g3,g4)
    c: Coincident(g4,g5)
    c: PointOnObject(g5,g-1)
    c: Vertical(g5)
    c: Coincident(g5,g6)
    c: Coincident(g6,g0)
FEATURE [PartDesign::Pad] Pad001
  Direction = (0,-1,2e-16)
  Length = 32.3
  Length2 = 10
  Placement = pos=(0,0,0) rot=(1,0,0;1.5708rad)
  Profile = -> Sketch001
  ReferenceAxis = -> Sketch001 [N_Axis]
  Refine = true
  Suppressed = false
  Type = 0
FEATURE [Sketcher::SketchObject] Sketch002
  AttachmentSupport = -> [Pad001]
  ExternalGeometry = -> [Pad001]
  FullyConstrained = true
  MapMode = 5
  Placement = pos=(-32.9638,0,0) rot=(0.707107,0,-0.707107;3.14159rad)
  sketch-geometry (6):
    g0: LineSegment StartX=-11.9502 StartY=32.3 StartZ=0 EndX=-8.29425 EndY=32.3 EndZ=0
    g1: LineSegment StartX=-8.29425 StartY=32.3 StartZ=0 EndX=-11.9502 EndY=28.47 EndZ=0
    g2: LineSegment StartX=-11.9502 StartY=28.47 StartZ=0 EndX=-11.9502 EndY=32.3 EndZ=0
    g3: LineSegment StartX=-11.9502 StartY=-2.7e-15 StartZ=0 EndX=-11.9502 EndY=3.83 EndZ=0
    g4: LineSegment StartX=-11.9502 StartY=3.83 StartZ=0 EndX=-8.29425 EndY=4e-16 EndZ=0
    g5: LineSegment StartX=-8.29425 StartY=4e-16 StartZ=0 EndX=-11.9502 EndY=-2.7e-15 EndZ=0
  constraints (14):
    c: Coincident(g-3,g0)
    c: Coincident(g0,g-4)
    c: Coincident(g0,g1)
    c: PointOnObject(g1,g-3)
    c: Coincident(g1,g2)
    c: Coincident(g2,g0)
    c: Coincident(g-3,g3)
    c: PointOnObject(g3,g-3)
    c: Coincident(g3,g4)
    c: Coincident(g4,g-4)
    c: Coincident(g4,g5)
    c: Coincident(g5,g3)
    c: Equal(g2,g3)
    c: DistanceY(g2,g2) = 3.83
FEATURE [PartDesign::Pocket] Pocket
  BaseFeature = -> Pad001
  Direction = (1,0,2e-16)
  Length = 5
  Length2 = 5
  Placement = pos=(0,0,0) rot=(1,0,0;1.5708rad)
  Profile = -> Sketch002
  ReferenceAxis = -> Sketch002 [N_Axis]
  Refine = true
  Suppressed = false
  Type = 1
FEATURE [PartDesign::Plane] DatumPlane
  AttachmentOffset = pos=(0,0,0) rot=(0,1,0;1.5708rad)
  AttachmentSupport = -> [Pocket]
  Length = 69.7141
  MapMode = 5
  Placement = pos=(1.68998,5.2e-15,11.6053) rot=(-0.654178,0,0.75634;3.14159rad)
  ResizeMode = 0
  Width = 68.8464
FEATURE [Sketcher::SketchObject] Sketch003
  AttachmentSupport = -> [DatumPlane]
  ExternalGeometry = -> [Pocket]
  FullyConstrained = true
  MapMode = 5
  Placement = pos=(1.68998,5.2e-15,11.6053) rot=(-0.654178,0,0.75634;3.14159rad)
  sketch-geometry (6):
    g0: LineSegment StartX=0 StartY=0 StartZ=0 EndX=0 EndY=3.83 EndZ=0
    g1: LineSegment StartX=0 StartY=3.83 StartZ=0 EndX=3.68434 EndY=-4e-16 EndZ=0
    g2: LineSegment StartX=3.68434 StartY=0 StartZ=0 EndX=0 EndY=0 EndZ=0
    g3: LineSegment StartX=-1.42e-14 StartY=28.47 StartZ=0 EndX=3.68434 EndY=32.3 EndZ=0
    g4: LineSegment StartX=3.68434 StartY=32.3 StartZ=0 EndX=0 EndY=32.3 EndZ=0
    g5: LineSegment StartX=0 StartY=32.3 StartZ=0 EndX=-1.42e-14 EndY=28.47 EndZ=0
  constraints (15):
    c: Coincident(g-1,g0)
    c: Vertical(g0)
    c: Coincident(g0,g1)
    c: Coincident(g1,g2)
    c: Horizontal(g2)
    c: Coincident(g3,g4)
    c: PointOnObject(g4,g-2)
    c: Coincident(g4,g5)
    c: Coincident(g5,g3)
    c: PointOnObject(g4,g-3)
    c: Equal(g2,g4)
    c: Equal(g5,g0)
    c: Coincident(g3,g-3)
    c: Coincident(g3,g-4)
    c: Coincident(g2,g0)
FEATURE [PartDesign::Pocket] Pocket001
  BaseFeature = -> Pocket
  Direction = (0.989563,0,-0.144102)
  Length = 30
  Length2 = 9
  Placement = pos=(0,0,0) rot=(1,0,0;1.5708rad)
  Profile = -> Sketch003
  ReferenceAxis = -> Sketch003 [N_Axis]
  Refine = true
  Suppressed = false
  Type = 4
FEATURE [Sketcher::SketchObject] Sketch004
  AttachmentSupport = -> [Pocket001]
  ExternalGeometry = -> [Pocket001]
  FullyConstrained = true
  MapMode = 5
  Placement = pos=(1.68998,5.2e-15,11.6053) rot=(0.07224,0,0.997387;3.14159rad)
  sketch-geometry (4):
    g0: LineSegment StartX=-21.6025 StartY=27.47 StartZ=0 EndX=-21.6025 EndY=4.83 EndZ=0
    g1: LineSegment StartX=-21.6025 StartY=4.83 StartZ=0 EndX=1.39341 EndY=4.83 EndZ=0
    g2: LineSegment StartX=1.39341 StartY=4.83 StartZ=0 EndX=1.39341 EndY=27.47 EndZ=0
    g3: LineSegment StartX=1.39341 StartY=27.47 StartZ=0 EndX=-21.6025 EndY=27.47 EndZ=0
  constraints (12):
    c: Coincident(g0,g1)
    c: Coincident(g1,g2)
    c: Coincident(g2,g3)
    c: Coincident(g3,g0)
    c: Vertical(g0)
    c: Vertical(g2)
    c: Horizontal(g1)
    c: Horizontal(g3)
    c: DistanceX(g-3,g0) = 1
    c: DistanceY(g0,g-3) = 1
    c: DistanceX(g1,g-4) = 1
    c: DistanceY(g-4,g1) = 1
FEATURE [PartDesign::Pocket] Pocket002
  BaseFeature = -> Pocket001
  Direction = (-0.144102,0,-0.989563)
  Length = 1
  Length2 = 5
  Placement = pos=(0,0,0) rot=(1,0,0;1.5708rad)
  Profile = -> Sketch004
  ReferenceAxis = -> Sketch004 [N_Axis]
  Refine = true
  Suppressed = false
  Type = 0
FEATURE [Sketcher::SketchObject] Sketch005
  AttachmentSupport = -> [Pocket002]
  ExternalGeometry = -> [Pocket002]
  FullyConstrained = true
  MapMode = 5
  Placement = pos=(0,5.3e-15,11.9502) rot=(0,0,1;3.14159rad)
  sketch-geometry (11):
    g0: LineSegment StartX=-21.397 StartY=15.43 StartZ=0 EndX=-21.397 EndY=6.83 EndZ=0
    g1: LineSegment StartX=-21.397 StartY=6.83 StartZ=0 EndX=-6.39705 EndY=6.83 EndZ=0
    g2: LineSegment StartX=-6.39705 StartY=6.83 StartZ=0 EndX=-6.39705 EndY=15.43 EndZ=0
    g3: LineSegment StartX=-6.39705 StartY=15.43 StartZ=0 EndX=-21.397 EndY=15.43 EndZ=0
    g4: LineSegment StartX=-21.397 StartY=25.47 StartZ=0 EndX=-21.397 EndY=16.87 EndZ=0
    g5: LineSegment StartX=-21.397 StartY=16.87 StartZ=0 EndX=-6.39705 EndY=16.87 EndZ=0
    g6: LineSegment StartX=-6.39705 StartY=16.87 StartZ=0 EndX=-6.39705 EndY=25.47 EndZ=0
    g7: LineSegment StartX=-6.39705 StartY=25.47 StartZ=0 EndX=-21.397 EndY=25.47 EndZ=0
    g8: LineSegment StartX=-21.397 StartY=16.87 StartZ=0 EndX=-21.397 EndY=15.43 EndZ=0
    g9: LineSegment StartX=-21.397 StartY=27.47 StartZ=0 EndX=-21.397 EndY=25.47 EndZ=0
    g10: LineSegment StartX=-21.397 StartY=4.83 StartZ=0 EndX=-21.397 EndY=6.83 EndZ=0
  constraints (32):
    c: Coincident(g0,g1)
    c: Coincident(g1,g2)
    c: Coincident(g3,g0)
    c: Vertical(g0)
    c: Vertical(g2)
    c: Horizontal(g1)
    c: Horizontal(g3)
    c: Coincident(g4,g5)
    c: Coincident(g5,g6)
    c: Coincident(g6,g7)
    c: Coincident(g7,g4)
    c: Vertical(g4)
    c: Vertical(g6)
    c: Horizontal(g5)
    c: Horizontal(g7)
    c: Coincident(g8,g4)
    c: Coincident(g8,g0)
    c: Vertical(g8)
    c: Equal(g4,g0)
    c: Equal(g5,g3)
    c: PointOnObject(g9,g-3)
    c: Coincident(g9,g4)
    c: PointOnObject(g10,g-4)
    c: Coincident(g10,g0)
    c: Vertical(g10)
    c: Equal(g9,g10)
    c: Vertical(g9)
    c: DistanceX(g-4,g10) = 1.67
    c: DistanceY(g-4,g0) = 2
    c: Coincident(g3,g2)
    c: DistanceY(g2,g2) = 8.6
    c: DistanceX(g1,g1) = 15
FEATURE [PartDesign::Pocket] Pocket003
  BaseFeature = -> Pocket002
  Direction = (0,0,-1)
  Length = 5
  Length2 = 5
  Placement = pos=(0,0,0) rot=(1,0,0;1.5708rad)
  Profile = -> Sketch005
  ReferenceAxis = -> Sketch005 [N_Axis]
  Refine = true
  Suppressed = false
  Type = 1
FEATURE [PartDesign::Fillet] Fillet
  Base = -> Pocket003 [Edge17,Edge45,Edge46,Edge23,Edge50,Edge49,Edge51,Edge47,Edge42,Edge44,Edge16,Edge21,Edge20,Edge25,Edge24,Edge18,Edge3,Edge2,Edge4,Edge43,Edge48,Edge22,Edge19]
  BaseFeature = -> Pocket003
  Placement = pos=(0,0,0) rot=(1,0,0;1.5708rad)
  Radius = 1.5
  Refine = true
  SupportTransform = false
  Suppressed = false
  UseAllEdges = false
FEATURE [Sketcher::SketchObject] Sketch006
  AttachmentSupport = -> [Fillet]
  ExternalGeometry = -> [Fillet]
  FullyConstrained = true
  MapMode = 5
  Placement = pos=(0,0,0) rot=(1,0,0;3.14159rad)
  sketch-geometry (6):
    g0: LineSegment StartX=-25.0623 StartY=27.4 StartZ=0 EndX=-25.0623 EndY=4.9 EndZ=0
    g1: LineSegment StartX=-25.0623 StartY=4.9 StartZ=0 EndX=26.9377 EndY=4.9 EndZ=0
    g2: LineSegment StartX=26.9377 StartY=4.9 StartZ=0 EndX=26.9377 EndY=27.4 EndZ=0
    g3: LineSegment StartX=26.9377 StartY=27.4 StartZ=0 EndX=-25.0623 EndY=27.4 EndZ=0
    g4: LineSegment StartX=-25.0623 StartY=27.4 StartZ=0 EndX=-25.0623 EndY=32.3 EndZ=0
    g5: LineSegment StartX=-25.0623 StartY=4.9 StartZ=0 EndX=-25.0623 EndY=0 EndZ=0
  constraints (18):
    c: Coincident(g0,g1)
    c: Coincident(g1,g2)
    c: Coincident(g2,g3)
    c: Coincident(g3,g0)
    c: Vertical(g0)
    c: Vertical(g2)
    c: Horizontal(g1)
    c: Horizontal(g3)
    c: DistanceX(g2,g-4) = 0.4
    c: Coincident(g4,g0)
    c: PointOnObject(g4,g-3)
    c: Vertical(g4)
    c: Coincident(g5,g0)
    c: PointOnObject(g5,g-1)
    c: Vertical(g5)
    c: Equal(g5,g4)
    c: DistanceX(g3,g3) = 52
    c: DistanceY(g0,g0) = 22.5
FEATURE [PartDesign::Pocket] Pocket004
  BaseFeature = -> Fillet
  Direction = (0,0,1)
  Length = 4
  Length2 = 5
  Placement = pos=(0,0,0) rot=(1,0,0;1.5708rad)
  Profile = -> Sketch006
  ReferenceAxis = -> Sketch006 [N_Axis]
  Refine = true
  Suppressed = false
  Type = 0
FEATURE [Sketcher::SketchObject] Sketch007
  AttachmentSupport = -> [Pocket004]
  ExternalGeometry = -> [Pocket004]
  FullyConstrained = true
  MapMode = 5
  Placement = pos=(27.3377,0,0) rot=(0.707107,0,0.707107;3.14159rad)
  sketch-geometry (6):
    g0: LineSegment StartX=0 StartY=20.4 StartZ=0 EndX=0 EndY=11.9 EndZ=0
    g1: LineSegment StartX=0 StartY=11.9 StartZ=0 EndX=3.63089 EndY=11.9 EndZ=0
    g2: LineSegment StartX=3.63089 StartY=11.9 StartZ=0 EndX=3.63089 EndY=20.4 EndZ=0
    g3: LineSegment StartX=3.63089 StartY=20.4 StartZ=0 EndX=0 EndY=20.4 EndZ=0
    g4: LineSegment StartX=3.63089 StartY=20.4 StartZ=0 EndX=3.63089 EndY=30.8 EndZ=0
    g5: LineSegment StartX=3.63089 StartY=11.9 StartZ=0 EndX=3.63089 EndY=1.5 EndZ=0
  constraints (16):
    c: Coincident(g0,g1)
    c: Coincident(g1,g2)
    c: Coincident(g2,g3)
    c: Coincident(g3,g0)
    c: Vertical(g0)
    c: Vertical(g2)
    c: Horizontal(g1)
    c: Horizontal(g3)
    c: PointOnObject(g0,g-2)
    c: PointOnObject(g1,g-3)
    c: Coincident(g4,g2)
    c: Coincident(g4,g-3)
    c: Coincident(g5,g1)
    c: Coincident(g5,g-3)
    c: Equal(g5,g4)
    c: DistanceY(g2,g2) = 8.5
FEATURE [PartDesign::Pocket] Pocket005
  BaseFeature = -> Pocket004
  Direction = (-1,0,2e-16)
  Length = 5
  Length2 = 5
  Placement = pos=(0,0,0) rot=(1,0,0;1.5708rad)
  Profile = -> Sketch007
  ReferenceAxis = -> Sketch007 [N_Axis]
  Refine = true
  Suppressed = false
  Type = 0
FEATURE [Sketcher::SketchObject] Sketch008
  AttachmentSupport = -> [Pocket005]
  ExternalGeometry = -> [Pocket005]
  FullyConstrained = true
  MapMode = 5
  Placement = pos=(0,0,4) rot=(1,0,0;3.14159rad)
  sketch-geometry (26):
    g0: LineSegment StartX=26.9377 StartY=23.9 StartZ=0 EndX=22.9377 EndY=23.9 EndZ=0
    g1: LineSegment StartX=22.9377 StartY=23.9 StartZ=0 EndX=22.9377 EndY=20.4 EndZ=0
    g2: LineSegment StartX=22.9377 StartY=20.4 StartZ=0 EndX=26.9377 EndY=20.4 EndZ=0
    g3: LineSegment StartX=26.9377 StartY=20.4 StartZ=0 EndX=26.9377 EndY=23.9 EndZ=0
    g4: LineSegment StartX=26.9377 StartY=11.9 StartZ=0 EndX=22.9377 EndY=11.9 EndZ=0
    g5: LineSegment StartX=22.9377 StartY=11.9 StartZ=0 EndX=22.9377 EndY=8.4 EndZ=0
    g6: LineSegment StartX=22.9377 StartY=8.4 StartZ=0 EndX=26.9377 EndY=8.4 EndZ=0
    g7: LineSegment StartX=26.9377 StartY=8.4 StartZ=0 EndX=26.9377 EndY=11.9 EndZ=0
    g8: Circle CenterX=24.5877 CenterY=21.85 CenterZ=0 NormalX=0 NormalY=0 NormalZ=1 AngleXU=0 Radius=0.75
    g9: Circle CenterX=24.5877 CenterY=10.45 CenterZ=0 NormalX=0 NormalY=0 NormalZ=1 AngleXU=0 Radius=0.75
    g10: LineSegment StartX=24.5877 StartY=21.85 StartZ=0 EndX=24.5877 EndY=20.4 EndZ=0
    g11: LineSegment StartX=24.5877 StartY=20.4 StartZ=0 EndX=24.5877 EndY=11.9 EndZ=0
    g12: LineSegment StartX=24.5877 StartY=11.9 StartZ=0 EndX=24.5877 EndY=10.45 EndZ=0
    g13: LineSegment StartX=24.5877 StartY=21.85 StartZ=0 EndX=-22.4123 EndY=21.85 EndZ=0
    g14: LineSegment StartX=-22.4123 StartY=21.85 StartZ=0 EndX=-22.4123 EndY=10.45 EndZ=0
    g15: LineSegment StartX=-22.4123 StartY=10.45 StartZ=0 EndX=24.5877 EndY=10.45 EndZ=0
    g16: Circle CenterX=-22.4123 CenterY=21.85 CenterZ=0 NormalX=0 NormalY=0 NormalZ=1 AngleXU=0 Radius=0.75
    g17: Circle CenterX=-22.4123 CenterY=10.45 CenterZ=0 NormalX=0 NormalY=0 NormalZ=1 AngleXU=0 Radius=0.75
    g18: LineSegment StartX=-25.0623 StartY=23.9 StartZ=0 EndX=-25.0623 EndY=20.4 EndZ=0
    g19: LineSegment StartX=-25.0623 StartY=20.4 StartZ=0 EndX=-20.3223 EndY=20.4 EndZ=0
    g20: LineSegment StartX=-20.3223 StartY=20.4 StartZ=0 EndX=-20.3223 EndY=23.9 EndZ=0
    g21: LineSegment StartX=-20.3223 StartY=23.9 StartZ=0 EndX=-25.0623 EndY=23.9 EndZ=0
    g22: LineSegment StartX=-25.0623 StartY=11.9 StartZ=0 EndX=-25.0623 EndY=8.4 EndZ=0
    g23: LineSegment StartX=-25.0623 StartY=8.4 StartZ=0 EndX=-20.3223 EndY=8.4 EndZ=0
    g24: LineSegment StartX=-20.3223 StartY=8.4 StartZ=0 EndX=-20.3223 EndY=11.9 EndZ=0
    g25: LineSegment StartX=-20.3223 StartY=11.9 StartZ=0 EndX=-25.0623 EndY=11.9 EndZ=0
  constraints (72):
    c: Coincident(g0,g1)
    c: Coincident(g1,g2)
    c: Coincident(g2,g3)
    c: Coincident(g3,g0)
    c: Horizontal(g0)
    c: Horizontal(g2)
    c: Vertical(g1)
    c: Coincident(g2,g-3)
    c: Coincident(g4,g5)
    c: Coincident(g5,g6)
    c: Coincident(g6,g7)
    c: Coincident(g7,g4)
    c: Horizontal(g4)
    c: Horizontal(g6)
    c: Vertical(g5)
    c: Vertical(g7)
    c: Coincident(g4,g-4)
    c: DistanceY(g5,g5) = 3.5
    c: Equal(g4,g2)
    c: DistanceX(g0,g0) = 4
    c: Vertical(g3)
    c: Equal(g1,g5)
    c: Coincident(g10,g8)
    c: PointOnObject(g10,g2)
    c: Vertical(g10)
    c: Coincident(g11,g10)
    c: PointOnObject(g11,g4)
    c: Vertical(g11)
    c: Coincident(g12,g11)
    c: Coincident(g12,g9)
    c: Vertical(g12)
    c: Equal(g12,g10)
    c: DistanceX(g4,g9) = 1.65
    c: Equal(g8,g9)
    c: Diameter(g8) = 1.5
    c: DistanceY(g10,g10) = 1.45
    c: Coincident(g13,g8)
    c: Horizontal(g13)
    c: Coincident(g14,g13)
    c: Vertical(g14)
    c: Coincident(g15,g14)
    c: Coincident(g15,g9)
    c: Horizontal(g15)
    c: Coincident(g16,g13)
    c: Coincident(g17,g14)
    c: Equal(g16,g17)
    c: Equal(g17,g8)
    c: DistanceX(g13,g13) = 47
    c: Coincident(g18,g19)
    c: Coincident(g19,g20)
    c: Coincident(g20,g21)
    c: Coincident(g21,g18)
    c: Vertical(g18)
    c: Vertical(g20)
    c: Horizontal(g19)
    c: Horizontal(g21)
    c: PointOnObject(g18,g-5)
    c: Coincident(g22,g23)
    c: Coincident(g23,g24)
    c: Coincident(g24,g25)
    c: Coincident(g25,g22)
    c: Vertical(g22)
    c: Vertical(g24)
    c: Horizontal(g23)
    c: Horizontal(g25)
    c: PointOnObject(g22,g-5)
    c: PointOnObject(g19,g2)
    c: PointOnObject(g24,g4)
    c: Equal(g20,g24)
    c: Equal(g24,g1)
    c: Equal(g19,g25)
    c: DistanceX(g19,g19) = 4.74
FEATURE [PartDesign::Pad] Pad002
  BaseFeature = -> Pocket005
  Direction = (0,0,-1)
  Length = 2.75
  Length2 = 10
  Placement = pos=(0,0,0) rot=(1,0,0;1.5708rad)
  Profile = -> Sketch008
  ReferenceAxis = -> Sketch008 [N_Axis]
  Refine = true
  Suppressed = false
  Type = 0
FEATURE [Sketcher::SketchObject] Sketch009
  AttachmentSupport = -> [Pad002]
  ExternalGeometry = -> [Pad002]
  FullyConstrained = true
  MapMode = 5
  Placement = pos=(0,0,4) rot=(1,0,0;3.14159rad)
  sketch-geometry (4):
    g0: LineSegment StartX=4.64705 StartY=26.47 StartZ=0 EndX=4.64705 EndY=5.83 EndZ=0
    g1: LineSegment StartX=4.64705 StartY=5.83 StartZ=0 EndX=22.897 EndY=5.83 EndZ=0
    g2: LineSegment StartX=22.897 StartY=5.83 StartZ=0 EndX=22.897 EndY=26.47 EndZ=0
    g3: LineSegment StartX=22.897 StartY=26.47 StartZ=0 EndX=4.64705 EndY=26.47 EndZ=0
  constraints (12):
    c: Coincident(g0,g1)
    c: Coincident(g1,g2)
    c: Coincident(g2,g3)
    c: Coincident(g3,g0)
    c: Vertical(g0)
    c: Vertical(g2)
    c: Horizontal(g1)
    c: Horizontal(g3)
    c: DistanceX(g0,g-3) = 1.75
    c: DistanceX(g-4,g2) = 1.5
    c: DistanceY(g-3,g0) = 1
    c: DistanceY(g0,g-5) = 1
FEATURE [PartDesign::Pocket] Pocket006
  BaseFeature = -> Pad002
  Direction = (0,0,1)
  Length = 1.5
  Length2 = 5
  Placement = pos=(0,0,0) rot=(1,0,0;1.5708rad)
  Profile = -> Sketch009
  ReferenceAxis = -> Sketch009 [N_Axis]
  Refine = true
  Suppressed = false
  Type = 0
FEATURE [PartDesign::Body] Body001  label="top"
  Group = -> [Sketch001,Pad001,Sketch002,Pocket,DatumPlane,Sketch003,Pocket001,Sketch004,Pocket002,Sketch005,Pocket003,Fillet,Sketch006,Pocket004,Sketch007,Pocket005,Sketch008,Pad002,Sketch009,Pocket006]
  Origin = -> Origin036
  Placement = pos=(0,-30.35,0) rot=(0,0,1;0rad)
  Tip = -> Pocket006
FEATURE [Sketcher::SketchObject] Sketch010
  AttachmentOffset = pos=(0,0,12) rot=(0,0,1;0rad)
  AttachmentSupport = -> [XY_Plane]
  ExternalGeometry = -> [Pad]
  FullyConstrained = true
  MapMode = 5
  Placement = pos=(0,0,12) rot=(0,0,1;0rad)
  sketch-geometry (6):
    g0: LineSegment StartX=5.20138 StartY=-7.8 StartZ=0 EndX=5.20138 EndY=-10.2 EndZ=0
    g1: LineSegment StartX=5.20138 StartY=-10.2 StartZ=0 EndX=22.6514 EndY=-10.2 EndZ=0
    g2: LineSegment StartX=22.6514 StartY=-10.2 StartZ=0 EndX=22.6514 EndY=-7.8 EndZ=0
    g3: LineSegment StartX=22.6514 StartY=-7.8 StartZ=0 EndX=5.20138 EndY=-7.8 EndZ=0
    g4: LineSegment StartX=5.20138 StartY=1.2e-15 StartZ=0 EndX=5.20138 EndY=-7.8 EndZ=0
    g5: LineSegment StartX=5.20138 StartY=-10.2 StartZ=0 EndX=5.20138 EndY=-18 EndZ=0
  constraints (16):
    c: Coincident(g0,g1)
    c: Coincident(g1,g2)
    c: Coincident(g2,g3)
    c: Coincident(g3,g0)
    c: Vertical(g0)
    c: Vertical(g2)
    c: Horizontal(g1)
    c: Horizontal(g3)
    c: PointOnObject(g0,g-3)
    c: PointOnObject(g1,g-4)
    c: Coincident(g4,g-3)
    c: Coincident(g4,g0)
    c: Coincident(g5,g0)
    c: Coincident(g5,g-3)
    c: Equal(g4,g5)
    c: DistanceY(g4,g4) = 7.8
FEATURE [PartDesign::Pocket] Pocket007
  BaseFeature = -> Pad
  Direction = (0,0,-1)
  Length = 6.75
  Length2 = 5
  Placement = pos=(0,0,0) rot=(1,0,0;1.5708rad)
  Profile = -> Sketch010
  ReferenceAxis = -> Sketch010 [N_Axis]
  Refine = true
  Suppressed = false
  Type = 0
FEATURE [PartDesign::Body] Body  label="Botons_vell"
  Group = -> [Sketch,Pad,Sketch010,Pocket007]
  Origin = -> Origin
  Placement = pos=(0,-37.5,0) rot=(0,0,1;0rad)
  Tip = -> Pocket007
FEATURE [Sketcher::SketchObject] Sketch011
  AttachmentSupport = -> [XY_Plane037]
  FullyConstrained = true
  MapMode = 5
  sketch-geometry (4):
    g0: LineSegment StartX=-32.96 StartY=0 StartZ=0 EndX=-32.96 EndY=-32.3 EndZ=0
    g1: LineSegment StartX=-32.96 StartY=-32.3 StartZ=0 EndX=27.34 EndY=-32.3 EndZ=0
    g2: LineSegment StartX=27.34 StartY=-32.3 StartZ=0 EndX=27.34 EndY=0 EndZ=0
    g3: LineSegment StartX=27.34 StartY=0 StartZ=0 EndX=-32.96 EndY=0 EndZ=0
  constraints (12):
    c: Coincident(g0,g1)
    c: Coincident(g1,g2)
    c: Coincident(g2,g3)
    c: Coincident(g3,g0)
    c: Vertical(g0)
    c: Vertical(g2)
    c: Horizontal(g1)
    c: Horizontal(g3)
    c: PointOnObject(g0,g-1)
    c: DistanceX(g1,g1) = 60.3
    c: DistanceX(g2) = 27.34
    c: DistanceY(g0,g0) = 32.3
FEATURE [PartDesign::Pad] Pad003
  Direction = (0,0,1)
  Length = 4.5
  Length2 = 10
  Profile = -> Sketch011
  ReferenceAxis = -> Sketch011 [N_Axis]
  Refine = true
  Reversed = true
  Suppressed = false
  TaperAngle = -40
  Type = 0
FEATURE [PartDesign::Fillet] Fillet001
  Base = -> Pad003 [Edge3,Edge4,Edge12,Edge7,Edge9,Edge10,Edge6,Edge2]
  BaseFeature = -> Pad003
  Radius = 2
  Refine = true
  SupportTransform = false
  Suppressed = false
  UseAllEdges = false
FEATURE [Sketcher::SketchObject] Sketch012
  AttachmentSupport = -> [Fillet001]
  ExternalGeometry = -> [Fillet001]
  FullyConstrained = true
  MapMode = 5
  Placement = pos=(0,0,-4.5) rot=(1,0,0;3.14159rad)
  sketch-geometry (35):
    g0: LineSegment StartX=4.38144 StartY=25.0914 StartZ=0 EndX=4.38144 EndY=21.5914 EndZ=0
    g1: LineSegment StartX=4.88144 StartY=21.0914 StartZ=0 EndX=16.6314 EndY=21.0914 EndZ=0
    g2: LineSegment StartX=17.1314 StartY=21.5914 StartZ=0 EndX=17.1314 EndY=25.0914 EndZ=0
    g3: LineSegment StartX=16.6314 StartY=25.5914 StartZ=0 EndX=4.88144 EndY=25.5914 EndZ=0
    g4: ArcOfCircle CenterX=4.88144 CenterY=25.0914 CenterZ=0 NormalX=0 NormalY=0 NormalZ=1 AngleXU=0 Radius=0.5 StartAngle=1.5708 EndAngle=3.14159
    g5: ArcOfCircle CenterX=4.88144 CenterY=21.5914 CenterZ=0 NormalX=0 NormalY=0 NormalZ=1 AngleXU=0 Radius=0.5 StartAngle=3.14159 EndAngle=4.71239
    g6: ArcOfCircle CenterX=16.6314 CenterY=21.5914 CenterZ=0 NormalX=0 NormalY=0 NormalZ=1 AngleXU=0 Radius=0.5 StartAngle=4.71239 EndAngle=6.28319
    g7: ArcOfCircle CenterX=16.6314 CenterY=25.0914 CenterZ=0 NormalX=0 NormalY=0 NormalZ=1 AngleXU=0 Radius=0.5 StartAngle=1.6e-15 EndAngle=1.5708
    g8: GeomPoint X=4.38144 Y=25.5914 Z=0
    g9: GeomPoint X=17.1314 Y=21.0914 Z=0
    g10: LineSegment StartX=4.38144 StartY=10.7086 StartZ=0 EndX=4.38144 EndY=7.20856 EndZ=0
    g11: LineSegment StartX=4.88144 StartY=6.70856 StartZ=0 EndX=16.6314 EndY=6.70856 EndZ=0
    g12: LineSegment StartX=17.1314 StartY=7.20856 StartZ=0 EndX=17.1314 EndY=10.7086 EndZ=0
    g13: LineSegment StartX=16.6314 StartY=11.2086 StartZ=0 EndX=4.88144 EndY=11.2086 EndZ=0
    g14: ArcOfCircle CenterX=4.88144 CenterY=10.7086 CenterZ=0 NormalX=0 NormalY=0 NormalZ=1 AngleXU=0 Radius=0.5 StartAngle=1.5708 EndAngle=3.14159
    g15: ArcOfCircle CenterX=4.88144 CenterY=7.20856 CenterZ=0 NormalX=0 NormalY=0 NormalZ=1 AngleXU=0 Radius=0.5 StartAngle=3.14159 EndAngle=4.71239
    g16: ArcOfCircle CenterX=16.6314 CenterY=7.20856 CenterZ=0 NormalX=0 NormalY=0 NormalZ=1 AngleXU=0 Radius=0.5 StartAngle=4.71239 EndAngle=6.28319
    g17: ArcOfCircle CenterX=16.6314 CenterY=10.7086 CenterZ=0 NormalX=0 NormalY=0 NormalZ=1 AngleXU=0 Radius=0.5 StartAngle=1.1e-15 EndAngle=1.5708
    g18: GeomPoint X=4.38144 Y=11.2086 Z=0
    g19: GeomPoint X=17.1314 Y=6.70856 Z=0
    g20: LineSegment StartX=-27.3514 StartY=22.025 StartZ=0 EndX=-27.3514 EndY=10.275 EndZ=0
    g21: LineSegment StartX=-26.8514 StartY=9.775 StartZ=0 EndX=-23.3514 EndY=9.775 EndZ=0
    g22: LineSegment StartX=-22.8514 StartY=10.275 StartZ=0 EndX=-22.8514 EndY=22.025 EndZ=0
    g23: LineSegment StartX=-23.3514 StartY=22.525 StartZ=0 EndX=-26.8514 EndY=22.525 EndZ=0
    g24: ArcOfCircle CenterX=-26.8514 CenterY=22.025 CenterZ=0 NormalX=0 NormalY=0 NormalZ=1 AngleXU=0 Radius=0.5 StartAngle=1.5708 EndAngle=3.14159
    g25: ArcOfCircle CenterX=-26.8514 CenterY=10.275 CenterZ=0 NormalX=0 NormalY=0 NormalZ=1 AngleXU=0 Radius=0.5 StartAngle=3.14159 EndAngle=4.71239
    g26: ArcOfCircle CenterX=-23.3514 CenterY=10.275 CenterZ=0 NormalX=0 NormalY=0 NormalZ=1 AngleXU=0 Radius=0.5 StartAngle=4.71239 EndAngle=6.28319
    g27: ArcOfCircle CenterX=-23.3514 CenterY=22.025 CenterZ=0 NormalX=0 NormalY=0 NormalZ=1 AngleXU=0 Radius=0.5 StartAngle=-2.7e-15 EndAngle=1.5708
    g28: GeomPoint X=-27.3514 Y=22.525 Z=0
    g29: GeomPoint X=-22.8514 Y=9.775 Z=0
    g30: LineSegment StartX=4.38144 StartY=25.5914 StartZ=0 EndX=4.38144 EndY=27.5914 EndZ=0
    g31: LineSegment StartX=17.1314 StartY=6.70856 StartZ=0 EndX=17.1314 EndY=4.70856 EndZ=0
    g32: LineSegment StartX=-26.8514 StartY=22.525 StartZ=0 EndX=-26.8514 EndY=27.5914 EndZ=0
    g33: LineSegment StartX=-26.8514 StartY=9.775 StartZ=0 EndX=-26.8514 EndY=4.70856 EndZ=0
    g34: LineSegment StartX=-27.3514 StartY=10.275 StartZ=0 EndX=-28.2514 EndY=10.275 EndZ=0
  constraints (87):
    c: Tangent(g0,g4) = -1.5708
    c: Tangent(g0,g5) = -1.5708
    c: Tangent(g1,g5) = -1.5708
    c: Tangent(g1,g6) = -1.5708
    c: Tangent(g2,g6) = -1.5708
    c: Tangent(g2,g7) = -1.5708
    c: Tangent(g3,g7) = -1.5708
    c: Tangent(g3,g4) = -1.5708
    c: Vertical(g0)
    c: Vertical(g2)
    c: Horizontal(g1)
    c: Horizontal(g3)
    c: Equal(g4,g5)
    c: Equal(g5,g6)
    c: Equal(g6,g7)
    c: PointOnObject(g8,g0)
    c: PointOnObject(g8,g3)
    c: PointOnObject(g9,g1)
    c: PointOnObject(g9,g2)
    c: Radius(g5) = 0.5
    c: Tangent(g10,g14) = -1.5708
    c: Tangent(g10,g15) = -1.5708
    c: Tangent(g11,g15) = -1.5708
    c: Tangent(g11,g16) = -1.5708
    c: Tangent(g12,g16) = -1.5708
    c: Tangent(g12,g17) = -1.5708
    c: Tangent(g13,g17) = -1.5708
    c: Tangent(g13,g14) = -1.5708
    c: Vertical(g10)
    c: Vertical(g12)
    c: Horizontal(g11)
    c: Horizontal(g13)
    c: Equal(g14,g15)
    c: Equal(g15,g16)
    c: Equal(g16,g17)
    c: PointOnObject(g18,g10)
    c: PointOnObject(g18,g13)
    c: PointOnObject(g19,g11)
    c: PointOnObject(g19,g12)
    c: Tangent(g20,g24) = -1.5708
    c: Tangent(g20,g25) = -1.5708
    c: Tangent(g21,g25) = -1.5708
    c: Tangent(g21,g26) = -1.5708
    c: Tangent(g22,g26) = -1.5708
    c: Tangent(g22,g27) = -1.5708
    c: Tangent(g23,g27) = -1.5708
    c: Tangent(g23,g24) = -1.5708
    c: Vertical(g20)
    c: Vertical(g22)
    c: Horizontal(g21)
    c: Horizontal(g23)
    c: Equal(g24,g25)
    c: Equal(g25,g26)
    c: Equal(g26,g27)
    c: PointOnObject(g28,g20)
    c: PointOnObject(g28,g23)
    c: PointOnObject(g29,g21)
    c: PointOnObject(g29,g22)
    c: Equal(g5,g15)
    c: Equal(g15,g25)
    c: PointOnObject(g10,g0)
    c: Equal(g1,g13)
    c: Equal(g10,g0)
    c: Equal(g1,g20)
    c: Equal(g2,g23)
    c: DistanceX(g0,g2) = 12.75
    c: DistanceY(g1,g3) = 4.5
    c: Coincident(g30,g8)
    c: PointOnObject(g30,g-3)
    c: Coincident(g31,g19)
    c: PointOnObject(g31,g-4)
    c: Vertical(g31)
    c: Vertical(g30)
    c: Equal(g30,g31)
    c: Coincident(g32,g23)
    c: PointOnObject(g32,g-3)
    c: Vertical(g32)
    c: Coincident(g33,g21)
    c: PointOnObject(g33,g-4)
    c: Vertical(g33)
    c: Equal(g33,g32)
    c: Coincident(g34,g20)
    c: PointOnObject(g34,g-6)
    c: Horizontal(g34)
    c: DistanceX(g34,g34) = 0.9
    c: DistanceX(g2,g-5) = 5.5
    c: DistanceY(g30,g30) = 2
FEATURE [PartDesign::Pad] Pad004
  BaseFeature = -> Fillet001
  Direction = (0,0,-1)
  Length = 0.5
  Length2 = 10
  Profile = -> Sketch012
  ReferenceAxis = -> Sketch012 [N_Axis]
  Refine = true
  Suppressed = false
  Type = 0
FEATURE [Sketcher::SketchObject] Sketch013
  AttachmentSupport = -> [Pad004]
  ExternalGeometry = -> [Pad004]
  FullyConstrained = true
  MapMode = 5
  Placement = pos=(0,0,-5) rot=(1,0,0;3.14159rad)
  sketch-geometry (30):
    g0: LineSegment StartX=4.78144 StartY=24.9414 StartZ=0 EndX=4.78144 EndY=21.7414 EndZ=0
    g1: LineSegment StartX=5.03144 StartY=21.4914 StartZ=0 EndX=16.4814 EndY=21.4914 EndZ=0
    g2: LineSegment StartX=16.7314 StartY=21.7414 StartZ=0 EndX=16.7314 EndY=24.9414 EndZ=0
    g3: LineSegment StartX=16.4814 StartY=25.1914 StartZ=0 EndX=5.03144 EndY=25.1914 EndZ=0
    g4: ArcOfCircle CenterX=5.03144 CenterY=24.9414 CenterZ=0 NormalX=0 NormalY=0 NormalZ=1 AngleXU=0 Radius=0.25 StartAngle=1.5708 EndAngle=3.14159
    g5: ArcOfCircle CenterX=5.03144 CenterY=21.7414 CenterZ=0 NormalX=0 NormalY=0 NormalZ=1 AngleXU=0 Radius=0.25 StartAngle=3.14159 EndAngle=4.71239
    g6: ArcOfCircle CenterX=16.4814 CenterY=21.7414 CenterZ=0 NormalX=0 NormalY=0 NormalZ=1 AngleXU=0 Radius=0.25 StartAngle=4.71239 EndAngle=6.28319
    g7: ArcOfCircle CenterX=16.4814 CenterY=24.9414 CenterZ=0 NormalX=0 NormalY=0 NormalZ=1 AngleXU=0 Radius=0.25 StartAngle=-5.3e-15 EndAngle=1.5708
    g8: GeomPoint X=4.78144 Y=25.1914 Z=0
    g9: GeomPoint X=16.7314 Y=21.4914 Z=0
    g10: LineSegment StartX=4.78144 StartY=10.5586 StartZ=0 EndX=4.78144 EndY=7.35856 EndZ=0
    g11: LineSegment StartX=5.03144 StartY=7.10856 StartZ=0 EndX=16.4814 EndY=7.10856 EndZ=0
    g12: LineSegment StartX=16.7314 StartY=7.35856 StartZ=0 EndX=16.7314 EndY=10.5586 EndZ=0
    g13: LineSegment StartX=16.4814 StartY=10.8086 StartZ=0 EndX=5.03144 EndY=10.8086 EndZ=0
    g14: ArcOfCircle CenterX=5.03144 CenterY=10.5586 CenterZ=0 NormalX=0 NormalY=0 NormalZ=1 AngleXU=0 Radius=0.25 StartAngle=1.5708 EndAngle=3.14159
    g15: ArcOfCircle CenterX=5.03144 CenterY=7.35856 CenterZ=0 NormalX=0 NormalY=0 NormalZ=1 AngleXU=0 Radius=0.25 StartAngle=3.14159 EndAngle=4.71239
    g16: ArcOfCircle CenterX=16.4814 CenterY=7.35856 CenterZ=0 NormalX=0 NormalY=0 NormalZ=1 AngleXU=0 Radius=0.25 StartAngle=4.71239 EndAngle=6.28319
    g17: ArcOfCircle CenterX=16.4814 CenterY=10.5586 CenterZ=0 NormalX=0 NormalY=0 NormalZ=1 AngleXU=0 Radius=0.25 StartAngle=1e-15 EndAngle=1.5708
    g18: GeomPoint X=4.78144 Y=10.8086 Z=0
    g19: GeomPoint X=16.7314 Y=7.10856 Z=0
    g20: LineSegment StartX=-26.9514 StartY=21.875 StartZ=0 EndX=-26.9514 EndY=10.425 EndZ=0
    g21: LineSegment StartX=-26.7014 StartY=10.175 StartZ=0 EndX=-23.5014 EndY=10.175 EndZ=0
    g22: LineSegment StartX=-23.2514 StartY=10.425 StartZ=0 EndX=-23.2514 EndY=21.875 EndZ=0
    g23: LineSegment StartX=-23.5014 StartY=22.125 StartZ=0 EndX=-26.7014 EndY=22.125 EndZ=0
    g24: ArcOfCircle CenterX=-26.7014 CenterY=21.875 CenterZ=0 NormalX=0 NormalY=0 NormalZ=1 AngleXU=0 Radius=0.25 StartAngle=1.5708 EndAngle=3.14159
    g25: ArcOfCircle CenterX=-26.7014 CenterY=10.425 CenterZ=0 NormalX=0 NormalY=0 NormalZ=1 AngleXU=0 Radius=0.25 StartAngle=3.14159 EndAngle=4.71239
    g26: ArcOfCircle CenterX=-23.5014 CenterY=10.425 CenterZ=0 NormalX=0 NormalY=0 NormalZ=1 AngleXU=0 Radius=0.25 StartAngle=4.71239 EndAngle=6.28319
    g27: ArcOfCircle CenterX=-23.5014 CenterY=21.875 CenterZ=0 NormalX=0 NormalY=0 NormalZ=1 AngleXU=0 Radius=0.25 StartAngle=5.1e-15 EndAngle=1.5708
    g28: GeomPoint X=-26.9514 Y=22.125 Z=0
    g29: GeomPoint X=-23.2514 Y=10.175 Z=0
  constraints (72):
    c: Tangent(g0,g4) = -1.5708
    c: Tangent(g0,g5) = -1.5708
    c: Tangent(g1,g5) = -1.5708
    c: Tangent(g1,g6) = -1.5708
    c: Tangent(g2,g6) = -1.5708
    c: Tangent(g2,g7) = -1.5708
    c: Tangent(g3,g7) = -1.5708
    c: Tangent(g3,g4) = -1.5708
    c: Vertical(g0)
    c: Vertical(g2)
    c: Horizontal(g1)
    c: Horizontal(g3)
    c: Equal(g4,g5)
    c: Equal(g5,g6)
    c: Equal(g6,g7)
    c: PointOnObject(g8,g0)
    c: PointOnObject(g8,g3)
    c: PointOnObject(g9,g1)
    c: PointOnObject(g9,g2)
    c: Radius(g5) = 0.25
    c: Tangent(g10,g14) = -1.5708
    c: Tangent(g10,g15) = -1.5708
    c: Tangent(g11,g15) = -1.5708
    c: Tangent(g11,g16) = -1.5708
    c: Tangent(g12,g16) = -1.5708
    c: Tangent(g12,g17) = -1.5708
    c: Tangent(g13,g17) = -1.5708
    c: Tangent(g13,g14) = -1.5708
    c: Vertical(g10)
    c: Vertical(g12)
    c: Horizontal(g11)
    c: Horizontal(g13)
    c: Equal(g14,g15)
    c: Equal(g15,g16)
    c: Equal(g16,g17)
    c: PointOnObject(g18,g10)
    c: PointOnObject(g18,g13)
    c: PointOnObject(g19,g11)
    c: PointOnObject(g19,g12)
    c: Radius(g15) = 0.25
    c: Tangent(g20,g24) = -1.5708
    c: Tangent(g20,g25) = -1.5708
    c: Tangent(g21,g25) = -1.5708
    c: Tangent(g21,g26) = -1.5708
    c: Tangent(g22,g26) = -1.5708
    c: Tangent(g22,g27) = -1.5708
    c: Tangent(g23,g27) = -1.5708
    c: Tangent(g23,g24) = -1.5708
    c: Vertical(g20)
    c: Vertical(g22)
    c: Horizontal(g21)
    c: Horizontal(g23)
    c: Equal(g24,g25)
    c: Equal(g25,g26)
    c: Equal(g26,g27)
    c: PointOnObject(g28,g20)
    c: PointOnObject(g28,g23)
    c: PointOnObject(g29,g21)
    c: PointOnObject(g29,g22)
    c: Radius(g25) = 0.25
    c: DistanceX(g-3,g8) = 0.4
    c: DistanceY(g8,g-4) = 0.4
    c: DistanceY(g-5,g9) = 0.4
    c: DistanceX(g9,g-6) = 0.4
    c: PointOnObject(g18,g0)
    c: PointOnObject(g12,g2)
    c: Equal(g10,g0)
    c: DistanceY(g13,g-7) = 0.4
    c: Equal(g2,g23)
    c: Equal(g13,g20)
    c: DistanceY(g23,g-8) = 0.4
    c: DistanceX(g-9,g28) = 0.4
FEATURE [Sketcher::SketchObject] Sketch014
  FullyConstrained = true
  MapMode = 5
  sketch-geometry (8):
    g0: LineSegment StartX=-22.41 StartY=-10.45 StartZ=0 EndX=-22.41 EndY=-21.85 EndZ=0
    g1: LineSegment StartX=-22.41 StartY=-21.85 StartZ=0 EndX=24.59 EndY=-21.85 EndZ=0
    g2: LineSegment StartX=24.59 StartY=-21.85 StartZ=0 EndX=24.59 EndY=-10.45 EndZ=0
    g3: LineSegment StartX=24.59 StartY=-10.45 StartZ=0 EndX=-22.41 EndY=-10.45 EndZ=0
    g4: Circle CenterX=-22.41 CenterY=-10.45 CenterZ=0 NormalX=0 NormalY=0 NormalZ=1 AngleXU=0 Radius=2
    g5: Circle CenterX=-22.41 CenterY=-21.85 CenterZ=0 NormalX=0 NormalY=0 NormalZ=1 AngleXU=0 Radius=2
    g6: Circle CenterX=24.59 CenterY=-10.45 CenterZ=0 NormalX=0 NormalY=0 NormalZ=1 AngleXU=0 Radius=2
    g7: Circle CenterX=24.59 CenterY=-21.85 CenterZ=0 NormalX=0 NormalY=0 NormalZ=1 AngleXU=0 Radius=2
  constraints (20):
    c: Coincident(g0,g1)
    c: Coincident(g1,g2)
    c: Coincident(g2,g3)
    c: Coincident(g3,g0)
    c: Vertical(g0)
    c: Vertical(g2)
    c: Horizontal(g1)
    c: Horizontal(g3)
    c: Coincident(g4,g0)
    c: Coincident(g5,g0)
    c: Coincident(g6,g2)
    c: Coincident(g7,g1)
    c: Equal(g4,g5)
    c: Equal(g5,g7)
    c: Equal(g7,g6)
    c: Diameter(g4) = 4
    c: DistanceX(g4) = -22.41
    c: DistanceY(g4) = -10.45
    c: DistanceX(g1,g1) = 47
    c: DistanceY(g2,g2) = 11.4
FEATURE [PartDesign::Pad] Pad005
  BaseFeature = -> Pad004
  Direction = (0,0,-1)
  Length = 0.4
  Length2 = 10
  Profile = -> Sketch013
  ReferenceAxis = -> Sketch013 [N_Axis]
  Refine = true
  Suppressed = false
  Type = 0
FEATURE [Sketcher::SketchObject] Sketch015
  FullyConstrained = true
  MapMode = 5
  sketch-geometry (8):
    g0: LineSegment StartX=-22.41 StartY=-10.45 StartZ=0 EndX=-22.41 EndY=-21.85 EndZ=0
    g1: LineSegment StartX=-22.41 StartY=-21.85 StartZ=0 EndX=24.59 EndY=-21.85 EndZ=0
    g2: LineSegment StartX=24.59 StartY=-21.85 StartZ=0 EndX=24.59 EndY=-10.45 EndZ=0
    g3: LineSegment StartX=24.59 StartY=-10.45 StartZ=0 EndX=-22.41 EndY=-10.45 EndZ=0
    g4: Circle CenterX=-22.41 CenterY=-10.45 CenterZ=0 NormalX=0 NormalY=0 NormalZ=1 AngleXU=0 Radius=2
    g5: Circle CenterX=-22.41 CenterY=-21.85 CenterZ=0 NormalX=0 NormalY=0 NormalZ=1 AngleXU=0 Radius=2
    g6: Circle CenterX=24.59 CenterY=-10.45 CenterZ=0 NormalX=0 NormalY=0 NormalZ=1 AngleXU=0 Radius=2
    g7: Circle CenterX=24.59 CenterY=-21.85 CenterZ=0 NormalX=0 NormalY=0 NormalZ=1 AngleXU=0 Radius=2
  constraints (20):
    c: Coincident(g0,g1)
    c: Coincident(g1,g2)
    c: Coincident(g2,g3)
    c: Coincident(g3,g0)
    c: Vertical(g0)
    c: Vertical(g2)
    c: Horizontal(g1)
    c: Horizontal(g3)
    c: Coincident(g4,g0)
    c: Coincident(g5,g0)
    c: Coincident(g6,g2)
    c: Coincident(g7,g1)
    c: Equal(g4,g5)
    c: Equal(g5,g7)
    c: Equal(g7,g6)
    c: Diameter(g4) = 4
    c: DistanceX(g4) = -22.41
    c: DistanceY(g4) = -10.45
    c: DistanceX(g1,g1) = 47
    c: DistanceY(g2,g2) = 11.4
FEATURE [PartDesign::Pocket] Pocket008
  BaseFeature = -> Pad005
  Direction = (0,0,-1)
  Length = 2
  Length2 = 5
  Profile = -> Sketch014
  ReferenceAxis = -> Sketch014 [N_Axis]
  Refine = true
  Suppressed = false
  Type = 0
FEATURE [PartDesign::Pocket] Pocket009
  BaseFeature = -> Pocket008
  Direction = (0,0,-1)
  Length = 1
  Length2 = 5
  Profile = -> Sketch015
  ReferenceAxis = -> Sketch015 [N_Axis]
  Refine = true
  Suppressed = false
  TaperAngle = -17.5
  Type = 0
FEATURE [PartDesign::Body] Body002  label="bottom"
  Group = -> [Sketch011,Pad003,Fillet001,Sketch012,Pad004,Sketch013,Sketch014,Pad005,Sketch015,Pocket008,Pocket009]
  Origin = -> Origin037
  Placement = pos=(0,-30.35,0) rot=(0,0,1;0rad)
  Tip = -> Pocket009
FEATURE [Sketcher::SketchObject] Sketch016
  AttachmentSupport = -> [XZ_Plane038]
  FullyConstrained = true
  MapMode = 5
  Placement = pos=(0,0,0) rot=(1,0,0;1.5708rad)
  sketch-geometry (14):
    g0: LineSegment StartX=21.1514 StartY=8.48067 StartZ=0 EndX=15.1514 EndY=9.36067 EndZ=0
    g1: LineSegment StartX=15.1514 StartY=9.36067 StartZ=0 EndX=15.1514 EndY=8.76067 EndZ=0
    g2: LineSegment StartX=15.1514 StartY=8.76067 StartZ=0 EndX=6.70138 EndY=10 EndZ=0
    g3: LineSegment StartX=6.70138 StartY=10 StartZ=0 EndX=6.70138 EndY=5.25 EndZ=0
    g4: LineSegment StartX=6.70138 StartY=5.25 StartZ=0 EndX=5.20138 EndY=5.25 EndZ=0
    g5: LineSegment StartX=5.20138 StartY=5.25 StartZ=0 EndX=5.20138 EndY=4.25 EndZ=0
    g6: LineSegment StartX=5.20138 StartY=4.25 StartZ=0 EndX=11.74 EndY=4.25 EndZ=0
    g7: LineSegment StartX=11.74 StartY=4.25 StartZ=0 EndX=11.74 EndY=3.5 EndZ=0
    g8: LineSegment StartX=11.74 StartY=3.5 StartZ=0 EndX=17.37 EndY=3.5 EndZ=0
    g9: LineSegment StartX=17.37 StartY=3.5 StartZ=0 EndX=17.37 EndY=4.25 EndZ=0
    g10: LineSegment StartX=17.37 StartY=4.25 StartZ=0 EndX=22.6514 EndY=4.25 EndZ=0
    g11: LineSegment StartX=22.6514 StartY=4.25 StartZ=0 EndX=22.6514 EndY=5.25 EndZ=0
    g12: LineSegment StartX=22.6514 StartY=5.25 StartZ=0 EndX=21.1514 EndY=5.25 EndZ=0
    g13: LineSegment StartX=21.1514 StartY=5.25 StartZ=0 EndX=21.1514 EndY=8.48067 EndZ=0
  constraints (42):
    c: Coincident(g0,g1)
    c: Vertical(g1)
    c: Coincident(g1,g2)
    c: Coincident(g2,g3)
    c: Vertical(g3)
    c: Coincident(g3,g4)
    c: Coincident(g4,g5)
    c: Vertical(g5)
    c: Coincident(g5,g6)
    c: Horizontal(g6)
    c: Coincident(g6,g7)
    c: Coincident(g7,g8)
    c: Horizontal(g8)
    c: Coincident(g8,g9)
    c: Coincident(g9,g10)
    c: Coincident(g10,g11)
    c: Vertical(g11)
    c: Coincident(g11,g12)
    c: Coincident(g12,g13)
    c: Coincident(g13,g0)
    c: Vertical(g13)
    c: Parallel(g0,g2)
    c: DistanceX(g0) = 21.1514
    c: DistanceX(g0,g0) = 6
    c: DistanceX(g2,g2) = 8.45
    c: DistanceY(g0,g0) = 0.88
    c: DistanceY(g1,g1) = 0.6
    c: Vertical(g9)
    c: Vertical(g7)
    c: Horizontal(g10)
    c: Equal(g7,g9)
    c: DistanceX(g7) = 11.74
    c: DistanceX(g8,g8) = 5.63
    c: DistanceX(g4,g3) = 1.5
    c: Horizontal(g12)
    c: DistanceX(g12,g12) = 1.5
    c: Horizontal(g4)
    c: PointOnObject(g3,g12)
    c: DistanceY(g5,g5) = 1
    c: DistanceY(g7,g7) = 0.75
    c: DistanceY(g3,g3) = 4.75
    c: DistanceY(g10) = 4.25
FEATURE [PartDesign::Pad] Pad006
  Direction = (0,-1,2e-16)
  Length = 18
  Length2 = 10
  Placement = pos=(0,0,0) rot=(1,0,0;1.5708rad)
  Profile = -> Sketch016
  ReferenceAxis = -> Sketch016 [N_Axis]
  Refine = true
  Suppressed = false
  Type = 0
FEATURE [Sketcher::SketchObject] Sketch017
  AttachmentOffset = pos=(0,0,12) rot=(0,0,1;0rad)
  AttachmentSupport = -> [XY_Plane038]
  ExternalGeometry = -> [Pad006]
  FullyConstrained = true
  MapMode = 5
  Placement = pos=(0,0,12) rot=(0,0,1;0rad)
  sketch-geometry (6):
    g0: LineSegment StartX=5.20138 StartY=-7.8 StartZ=0 EndX=5.20138 EndY=-10.2 EndZ=0
    g1: LineSegment StartX=5.20138 StartY=-10.2 StartZ=0 EndX=22.6514 EndY=-10.2 EndZ=0
    g2: LineSegment StartX=22.6514 StartY=-10.2 StartZ=0 EndX=22.6514 EndY=-7.8 EndZ=0
    g3: LineSegment StartX=22.6514 StartY=-7.8 StartZ=0 EndX=5.20138 EndY=-7.8 EndZ=0
    g4: LineSegment StartX=5.20138 StartY=1.2e-15 StartZ=0 EndX=5.20138 EndY=-7.8 EndZ=0
    g5: LineSegment StartX=5.20138 StartY=-10.2 StartZ=0 EndX=5.20138 EndY=-18 EndZ=0
  constraints (16):
    c: Coincident(g0,g1)
    c: Coincident(g1,g2)
    c: Coincident(g2,g3)
    c: Coincident(g3,g0)
    c: Vertical(g0)
    c: Vertical(g2)
    c: Horizontal(g1)
    c: Horizontal(g3)
    c: PointOnObject(g0,g-3)
    c: PointOnObject(g1,g-4)
    c: Coincident(g4,g-3)
    c: Coincident(g4,g0)
    c: Coincident(g5,g0)
    c: Coincident(g5,g-3)
    c: Equal(g4,g5)
    c: DistanceY(g4,g4) = 7.8
FEATURE [PartDesign::Pocket] Pocket010
  BaseFeature = -> Pad006
  Direction = (0,0,-1)
  Length = 6.75
  Length2 = 5
  Placement = pos=(0,0,0) rot=(1,0,0;1.5708rad)
  Profile = -> Sketch017
  ReferenceAxis = -> Sketch017 [N_Axis]
  Refine = true
  Suppressed = false
  Type = 0
FEATURE [Sketcher::SketchObject] Sketch018
  AttachmentSupport = -> [Pocket010]
  ExternalGeometry = -> [Pocket010]
  FullyConstrained = true
  MapMode = 5
  Placement = pos=(0,8e-16,3.5) rot=(1,0,0;3.14159rad)
  sketch-geometry (4):
    g0: LineSegment StartX=11.74 StartY=18 StartZ=0 EndX=11.74 EndY=10.2 EndZ=0
    g1: LineSegment StartX=11.74 StartY=10.2 StartZ=0 EndX=17.37 EndY=10.2 EndZ=0
    g2: LineSegment StartX=17.37 StartY=10.2 StartZ=0 EndX=17.37 EndY=18 EndZ=0
    g3: LineSegment StartX=17.37 StartY=18 StartZ=0 EndX=11.74 EndY=18 EndZ=0
  constraints (10):
    c: Coincident(g0,g1)
    c: Coincident(g1,g2)
    c: Coincident(g2,g3)
    c: Coincident(g3,g0)
    c: Vertical(g0)
    c: Vertical(g2)
    c: Horizontal(g1)
    c: Coincident(g0,g-3)
    c: PointOnObject(g1,g-4)
    c: Coincident(g2,g-3)
FEATURE [PartDesign::Pad] Pad007
  BaseFeature = -> Pocket010
  Direction = (0,0,-1)
  Length = 0.66
  Length2 = 10
  Placement = pos=(0,0,0) rot=(1,0,0;1.5708rad)
  Profile = -> Sketch018
  ReferenceAxis = -> Sketch018 [N_Axis]
  Refine = true
  Suppressed = false
  Type = 0
FEATURE [PartDesign::Body] Body003  label="Botons_vell001"
  Group = -> [Sketch016,Pad006,Sketch017,Pocket010,Sketch018,Pad007]
  Origin = -> Origin038
  Placement = pos=(0,-37.5,0) rot=(0,0,1;0rad)
  Tip = -> Pad007
